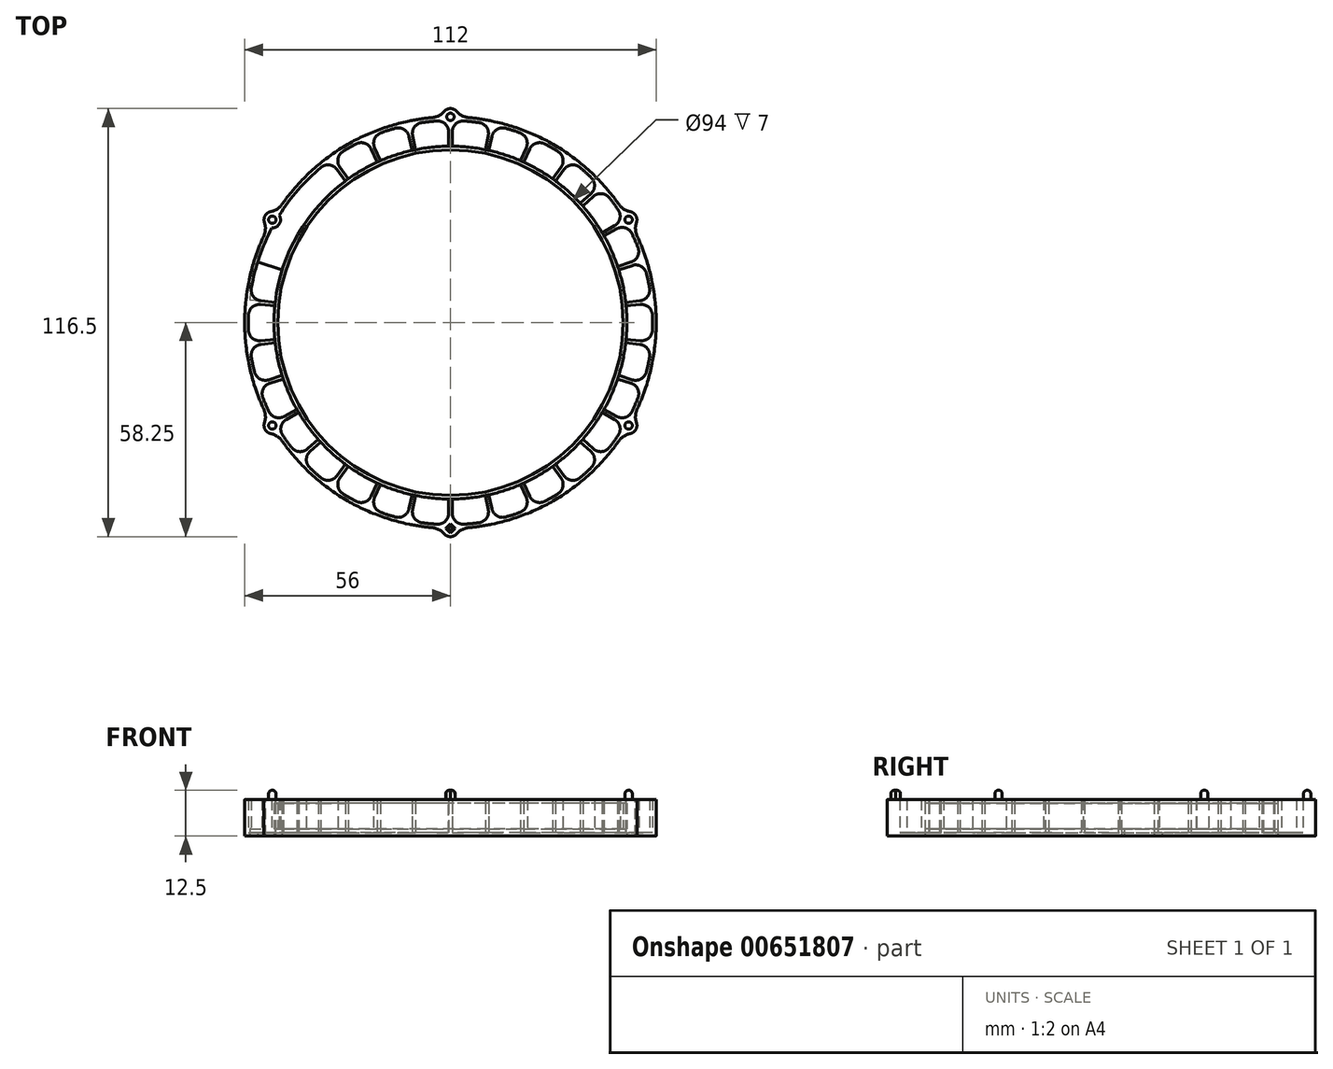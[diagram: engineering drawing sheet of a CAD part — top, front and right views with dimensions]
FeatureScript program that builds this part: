
annotation { "Feature Type Name" : "Feature", "Feature Type Description" : "" }
export const myFeature = defineFeature(function(context is Context, id is Id, definition is map)
    precondition{}
    {
        {
            var Q0;
            Q0=qCreatedBy(makeId("Top.planeOp"),FACE);
            var sketch = newSketch(context, id + "F0", { "sketchPlane" : qUnion([Q0])});
            skCircle(sketch, "E0", {"center": v(0, 0) * mm, "radius": 55 * mm});
            skCircle(sketch, "E1", {"center": v(0, 0) * mm, "radius": 56 * mm});
            skLineSegment(sketch, "E2", {"start": v(0, 60.2) * mm, "end": v(0, -62.26) * mm, "construction": true});
            skLineSegment(sketch, "E3", {"start": v(-62.84, 0) * mm, "end": v(64.36, 0) * mm, "construction": true});
            skLineSegment(sketch, "E4", {"start": v(55, 0) * mm, "end": v(56, 0) * mm});
            skCircle(sketch, "E5", {"center": v(0, 0) * mm, "radius": 48 * mm});
            skCircle(sketch, "E6", {"center": v(0, 0) * mm, "radius": 47 * mm});
            skLineSegment(sketch, "E7.left", {"start": v(-56, 0.5) * mm, "end": v(-56, -0.5) * mm});
            skLineSegment(sketch, "E7.right", {"start": v(56, 0.5) * mm, "end": v(56, -0.5) * mm});
            skLineSegment(sketch, "E8.bottom", {"start": v(0.5, -56) * mm, "end": v(-0.5, -56) * mm});
            skLineSegment(sketch, "E8.top", {"start": v(0.5, 56) * mm, "end": v(-0.5, 56) * mm});
            skLineSegment(sketch, "E8.left", {"start": v(0.5, -56) * mm, "end": v(0.5, 56) * mm});
            skLineSegment(sketch, "E8.right", {"start": v(-0.5, -56) * mm, "end": v(-0.5, 56) * mm});
            skLineSegment(sketch, "E9.bottom", {"start": v(12.13, 54.67) * mm, "end": v(-11.15, -54.88) * mm});
            skLineSegment(sketch, "E9.top", {"start": v(11.15, 54.88) * mm, "end": v(-12.13, -54.67) * mm});
            skLineSegment(sketch, "E9.left", {"start": v(12.13, 54.67) * mm, "end": v(11.15, 54.88) * mm});
            skLineSegment(sketch, "E9.right", {"start": v(-11.15, -54.88) * mm, "end": v(-12.13, -54.67) * mm});
            skLineSegment(sketch, "E10.bottom", {"start": v(-22.32, -51.36) * mm, "end": v(-23.23, -50.95) * mm});
            skLineSegment(sketch, "E10.top", {"start": v(23.23, 50.95) * mm, "end": v(22.32, 51.36) * mm});
            skLineSegment(sketch, "E10.left", {"start": v(-22.32, -51.36) * mm, "end": v(23.23, 50.95) * mm});
            skLineSegment(sketch, "E10.right", {"start": v(-23.23, -50.95) * mm, "end": v(22.32, 51.36) * mm});
            skLineSegment(sketch, "E11.bottom", {"start": v(32.51, 45.6) * mm, "end": v(33.32, 45) * mm});
            skLineSegment(sketch, "E11.top", {"start": v(-33.32, -45) * mm, "end": v(-32.51, -45.6) * mm});
            skLineSegment(sketch, "E11.left", {"start": v(32.51, 45.6) * mm, "end": v(-33.32, -45) * mm});
            skLineSegment(sketch, "E11.right", {"start": v(33.32, 45) * mm, "end": v(-32.51, -45.6) * mm});
            skLineSegment(sketch, "E12.bottom", {"start": v(-41.28, -37.84) * mm, "end": v(-41.95, -37.1) * mm});
            skLineSegment(sketch, "E12.top", {"start": v(41.95, 37.1) * mm, "end": v(41.28, 37.84) * mm});
            skLineSegment(sketch, "E12.left", {"start": v(-41.28, -37.84) * mm, "end": v(41.95, 37.1) * mm});
            skLineSegment(sketch, "E12.right", {"start": v(-41.95, -37.1) * mm, "end": v(41.28, 37.84) * mm});
            skLineSegment(sketch, "E13.bottom", {"start": v(48.25, 28.43) * mm, "end": v(48.75, 27.57) * mm});
            skLineSegment(sketch, "E13.top", {"start": v(-48.75, -27.57) * mm, "end": v(-48.25, -28.43) * mm});
            skLineSegment(sketch, "E13.left", {"start": v(48.25, 28.43) * mm, "end": v(-48.75, -27.57) * mm});
            skLineSegment(sketch, "E13.right", {"start": v(48.75, 27.57) * mm, "end": v(-48.25, -28.43) * mm});
            skLineSegment(sketch, "E14.bottom", {"start": v(-53.1, -17.78) * mm, "end": v(-53.41, -16.83) * mm});
            skLineSegment(sketch, "E14.top", {"start": v(53.41, 16.83) * mm, "end": v(53.1, 17.78) * mm});
            skLineSegment(sketch, "E14.left", {"start": v(-53.1, -17.78) * mm, "end": v(53.41, 16.83) * mm});
            skLineSegment(sketch, "E14.right", {"start": v(-53.41, -16.83) * mm, "end": v(53.1, 17.78) * mm});
            skLineSegment(sketch, "E15.bottom", {"start": v(55.64, 6.35) * mm, "end": v(55.74, 5.36) * mm});
            skLineSegment(sketch, "E15.top", {"start": v(-55.74, -5.36) * mm, "end": v(-55.64, -6.35) * mm});
            skLineSegment(sketch, "E15.left", {"start": v(55.64, 6.35) * mm, "end": v(-55.74, -5.36) * mm});
            skLineSegment(sketch, "E15.right", {"start": v(55.74, 5.36) * mm, "end": v(-55.64, -6.35) * mm});
            skLineSegment(sketch, "E16.bottom", {"start": v(-55.74, 5.36) * mm, "end": v(-55.64, 6.35) * mm});
            skLineSegment(sketch, "E16.top", {"start": v(55.64, -6.35) * mm, "end": v(55.74, -5.36) * mm});
            skLineSegment(sketch, "E16.left", {"start": v(-55.74, 5.36) * mm, "end": v(55.64, -6.35) * mm});
            skLineSegment(sketch, "E16.right", {"start": v(-55.64, 6.35) * mm, "end": v(55.74, -5.36) * mm});
            skLineSegment(sketch, "E17.bottom", {"start": v(53.41, -16.83) * mm, "end": v(53.1, -17.78) * mm});
            skLineSegment(sketch, "E17.top", {"start": v(-53.1, 17.78) * mm, "end": v(-53.41, 16.83) * mm});
            skLineSegment(sketch, "E17.left", {"start": v(53.41, -16.83) * mm, "end": v(-53.1, 17.78) * mm});
            skLineSegment(sketch, "E17.right", {"start": v(53.1, -17.78) * mm, "end": v(-53.41, 16.83) * mm});
            skLineSegment(sketch, "E18.bottom", {"start": v(48.75, -27.57) * mm, "end": v(48.25, -28.43) * mm});
            skLineSegment(sketch, "E18.top", {"start": v(-48.25, 28.43) * mm, "end": v(-48.75, 27.57) * mm});
            skLineSegment(sketch, "E18.left", {"start": v(48.75, -27.57) * mm, "end": v(-48.25, 28.43) * mm});
            skLineSegment(sketch, "E18.right", {"start": v(48.25, -28.43) * mm, "end": v(-48.75, 27.57) * mm});
            skLineSegment(sketch, "E19.bottom", {"start": v(-41.95, 37.1) * mm, "end": v(-41.28, 37.84) * mm});
            skLineSegment(sketch, "E19.top", {"start": v(41.28, -37.84) * mm, "end": v(41.95, -37.1) * mm});
            skLineSegment(sketch, "E19.left", {"start": v(-41.95, 37.1) * mm, "end": v(41.28, -37.84) * mm});
            skLineSegment(sketch, "E19.right", {"start": v(-41.28, 37.84) * mm, "end": v(41.95, -37.1) * mm});
            skLineSegment(sketch, "E20.bottom", {"start": v(-33.32, 45) * mm, "end": v(-32.51, 45.6) * mm});
            skLineSegment(sketch, "E20.top", {"start": v(32.51, -45.6) * mm, "end": v(33.32, -45) * mm});
            skLineSegment(sketch, "E20.left", {"start": v(-33.32, 45) * mm, "end": v(32.51, -45.6) * mm});
            skLineSegment(sketch, "E20.right", {"start": v(-32.51, 45.6) * mm, "end": v(33.32, -45) * mm});
            skLineSegment(sketch, "E21.bottom", {"start": v(-23.23, 50.95) * mm, "end": v(-22.32, 51.36) * mm});
            skLineSegment(sketch, "E21.top", {"start": v(22.32, -51.36) * mm, "end": v(23.23, -50.95) * mm});
            skLineSegment(sketch, "E21.left", {"start": v(-23.23, 50.95) * mm, "end": v(22.32, -51.36) * mm});
            skLineSegment(sketch, "E21.right", {"start": v(-22.32, 51.36) * mm, "end": v(23.23, -50.95) * mm});
            skLineSegment(sketch, "E22.bottom", {"start": v(-12.13, 54.67) * mm, "end": v(-11.15, 54.88) * mm});
            skLineSegment(sketch, "E22.top", {"start": v(11.15, -54.88) * mm, "end": v(12.13, -54.67) * mm});
            skLineSegment(sketch, "E22.left", {"start": v(-12.13, 54.67) * mm, "end": v(11.15, -54.88) * mm});
            skLineSegment(sketch, "E22.right", {"start": v(-11.15, 54.88) * mm, "end": v(12.13, -54.67) * mm});
            skSolve(sketch);
        }
        {
            var Q0;
            {var subQ0=sQuery(id+"F0.wireOp",EDGE,"E7.left");Q0=makeQuery(id+"F0.imprint","IMPRINT",FACE,{"disambiguationData":[TD([[makeQuery(id+"F0.imprint","IMPRINT",EDGE,{"derivedFrom":subQ0}),1.0]])]});}
            var Q1;
            {var subQ5=sQuery(id+"F0.wireOp",EDGE,"E8.top");Q1=makeQuery(id+"F0.imprint","IMPRINT",FACE,{"disambiguationData":[TD([[makeQuery(id+"F0.imprint","IMPRINT",EDGE,{"derivedFrom":subQ5}),1.0]])]});}
            var Q2;
            {var subQ0=sQuery(id+"F0.wireOp",EDGE,"E9.top");var subQ1=sQuery(id+"F0.wireOp",EDGE,"E0");var subQ2=makeQuery(id+"F0.imprint","INTERSECT",VERTEX,{"disambiguationData":[OD(0.0)],"derivedFrom":[subQ1,subQ0]});Q2=makeQuery(id+"F0.imprint","IMPRINT",FACE,{"disambiguationData":[TD([[makeQuery(id+"F0.imprint","IMPRINT",EDGE,{"disambiguationData":[TD([[subQ2,-1.0]])],"derivedFrom":subQ1}),-1.0]])]});}
            var Q3;
            {var subQ5=sQuery(id+"F0.wireOp",EDGE,"E9.left");Q3=makeQuery(id+"F0.imprint","IMPRINT",FACE,{"disambiguationData":[TD([[makeQuery(id+"F0.imprint","IMPRINT",EDGE,{"derivedFrom":subQ5}),1.0]])]});}
            var Q4;
            {var subQ0=sQuery(id+"F0.wireOp",EDGE,"E10.right");var subQ1=sQuery(id+"F0.wireOp",EDGE,"E0");var subQ2=makeQuery(id+"F0.imprint","INTERSECT",VERTEX,{"disambiguationData":[OD(0.0)],"derivedFrom":[subQ1,subQ0]});Q4=makeQuery(id+"F0.imprint","IMPRINT",FACE,{"disambiguationData":[TD([[makeQuery(id+"F0.imprint","IMPRINT",EDGE,{"disambiguationData":[TD([[subQ2,-1.0]])],"derivedFrom":subQ1}),-1.0]])]});}
            var Q5;
            {var subQ5=sQuery(id+"F0.wireOp",EDGE,"E10.top");Q5=makeQuery(id+"F0.imprint","IMPRINT",FACE,{"disambiguationData":[TD([[makeQuery(id+"F0.imprint","IMPRINT",EDGE,{"derivedFrom":subQ5}),1.0]])]});}
            var Q6;
            {var subQ0=sQuery(id+"F0.wireOp",EDGE,"E11.left");var subQ1=sQuery(id+"F0.wireOp",EDGE,"E0");var subQ2=makeQuery(id+"F0.imprint","INTERSECT",VERTEX,{"disambiguationData":[OD(0.0)],"derivedFrom":[subQ1,subQ0]});Q6=makeQuery(id+"F0.imprint","IMPRINT",FACE,{"disambiguationData":[TD([[makeQuery(id+"F0.imprint","IMPRINT",EDGE,{"disambiguationData":[TD([[subQ2,-1.0]])],"derivedFrom":subQ1}),-1.0]])]});}
            var Q7;
            {var subQ3=sQuery(id+"F0.wireOp",EDGE,"E4");var subQ7=sQuery(id+"F0.wireOp",EDGE,"E0");var subQ8=makeQuery(id+"F0.imprint","INTERSECT",VERTEX,{"derivedFrom":[subQ7,subQ3]});Q7=makeQuery(id+"F0.imprint","IMPRINT",FACE,{"disambiguationData":[TD([[makeQuery(id+"F0.imprint","IMPRINT",EDGE,{"disambiguationData":[TD([[subQ8,-1.0]])],"derivedFrom":subQ7}),-1.0]])]});}
            var Q8;
            {var subQ5=sQuery(id+"F0.wireOp",EDGE,"E11.bottom");Q8=makeQuery(id+"F0.imprint","IMPRINT",FACE,{"disambiguationData":[TD([[makeQuery(id+"F0.imprint","IMPRINT",EDGE,{"derivedFrom":subQ5}),-1.0]])]});}
            var Q9;
            {var subQ3=sQuery(id+"F0.wireOp",EDGE,"E4");var subQ5=sQuery(id+"F0.wireOp",EDGE,"E0");var subQ6=makeQuery(id+"F0.imprint","INTERSECT",VERTEX,{"derivedFrom":[subQ5,subQ3]});Q9=makeQuery(id+"F0.imprint","IMPRINT",FACE,{"disambiguationData":[TD([[makeQuery(id+"F0.imprint","IMPRINT",EDGE,{"disambiguationData":[TD([[subQ6,1.0]])],"derivedFrom":subQ5}),-1.0]])]});}
            var Q10;
            {var subQ5=sQuery(id+"F0.wireOp",EDGE,"E8.bottom");Q10=makeQuery(id+"F0.imprint","IMPRINT",FACE,{"disambiguationData":[TD([[makeQuery(id+"F0.imprint","IMPRINT",EDGE,{"derivedFrom":subQ5}),-1.0]])]});}
            var Q11;
            {var subQ0=sQuery(id+"F0.wireOp",EDGE,"E11.right");var subQ1=sQuery(id+"F0.wireOp",EDGE,"E0");var subQ2=makeQuery(id+"F0.imprint","INTERSECT",VERTEX,{"disambiguationData":[OD(1.0)],"derivedFrom":[subQ1,subQ0]});Q11=makeQuery(id+"F0.imprint","IMPRINT",FACE,{"disambiguationData":[TD([[makeQuery(id+"F0.imprint","IMPRINT",EDGE,{"disambiguationData":[TD([[subQ2,-1.0]])],"derivedFrom":subQ1}),-1.0]])]});}
            var Q12;
            {var subQ5=sQuery(id+"F0.wireOp",EDGE,"E11.top");Q12=makeQuery(id+"F0.imprint","IMPRINT",FACE,{"disambiguationData":[TD([[makeQuery(id+"F0.imprint","IMPRINT",EDGE,{"derivedFrom":subQ5}),1.0]])]});}
            var Q13;
            {var subQ5=sQuery(id+"F0.wireOp",EDGE,"E10.bottom");Q13=makeQuery(id+"F0.imprint","IMPRINT",FACE,{"disambiguationData":[TD([[makeQuery(id+"F0.imprint","IMPRINT",EDGE,{"derivedFrom":subQ5}),-1.0]])]});}
            var Q14;
            {var subQ0=sQuery(id+"F0.wireOp",EDGE,"E10.left");var subQ1=sQuery(id+"F0.wireOp",EDGE,"E0");var subQ2=makeQuery(id+"F0.imprint","INTERSECT",VERTEX,{"disambiguationData":[OD(1.0)],"derivedFrom":[subQ1,subQ0]});Q14=makeQuery(id+"F0.imprint","IMPRINT",FACE,{"disambiguationData":[TD([[makeQuery(id+"F0.imprint","IMPRINT",EDGE,{"disambiguationData":[TD([[subQ2,-1.0]])],"derivedFrom":subQ1}),-1.0]])]});}
            var Q15;
            {var subQ5=sQuery(id+"F0.wireOp",EDGE,"E9.right");Q15=makeQuery(id+"F0.imprint","IMPRINT",FACE,{"disambiguationData":[TD([[makeQuery(id+"F0.imprint","IMPRINT",EDGE,{"derivedFrom":subQ5}),-1.0]])]});}
            var Q16;
            {var subQ0=sQuery(id+"F0.wireOp",EDGE,"E9.bottom");var subQ1=sQuery(id+"F0.wireOp",EDGE,"E0");var subQ2=makeQuery(id+"F0.imprint","INTERSECT",VERTEX,{"disambiguationData":[OD(1.0)],"derivedFrom":[subQ1,subQ0]});Q16=makeQuery(id+"F0.imprint","IMPRINT",FACE,{"disambiguationData":[TD([[makeQuery(id+"F0.imprint","IMPRINT",EDGE,{"disambiguationData":[TD([[subQ2,-1.0]])],"derivedFrom":subQ1}),-1.0]])]});}
            var Q17;
            {var subQ0=sQuery(id+"F0.wireOp",EDGE,"E8.left");var subQ1=sQuery(id+"F0.wireOp",EDGE,"E0");var subQ2=makeQuery(id+"F0.imprint","INTERSECT",VERTEX,{"disambiguationData":[OD(0.0)],"derivedFrom":[subQ1,subQ0]});Q17=makeQuery(id+"F0.imprint","IMPRINT",FACE,{"disambiguationData":[TD([[makeQuery(id+"F0.imprint","IMPRINT",EDGE,{"disambiguationData":[TD([[subQ2,-1.0]])],"derivedFrom":subQ1}),1.0]])]});}
            var Q18;
            {var subQ0=sQuery(id+"F0.wireOp",EDGE,"E9.bottom");var subQ1=sQuery(id+"F0.wireOp",EDGE,"E0");var subQ2=makeQuery(id+"F0.imprint","INTERSECT",VERTEX,{"disambiguationData":[OD(0.0)],"derivedFrom":[subQ1,subQ0]});Q18=makeQuery(id+"F0.imprint","IMPRINT",FACE,{"disambiguationData":[TD([[makeQuery(id+"F0.imprint","IMPRINT",EDGE,{"disambiguationData":[TD([[subQ2,-1.0]])],"derivedFrom":subQ1}),1.0]])]});}
            var Q19;
            {var subQ0=sQuery(id+"F0.wireOp",EDGE,"E10.left");var subQ1=sQuery(id+"F0.wireOp",EDGE,"E0");var subQ2=makeQuery(id+"F0.imprint","INTERSECT",VERTEX,{"disambiguationData":[OD(0.0)],"derivedFrom":[subQ1,subQ0]});Q19=makeQuery(id+"F0.imprint","IMPRINT",FACE,{"disambiguationData":[TD([[makeQuery(id+"F0.imprint","IMPRINT",EDGE,{"disambiguationData":[TD([[subQ2,-1.0]])],"derivedFrom":subQ1}),1.0]])]});}
            var Q20;
            {var subQ0=sQuery(id+"F0.wireOp",EDGE,"E11.right");var subQ1=sQuery(id+"F0.wireOp",EDGE,"E0");var subQ2=makeQuery(id+"F0.imprint","INTERSECT",VERTEX,{"disambiguationData":[OD(0.0)],"derivedFrom":[subQ1,subQ0]});Q20=makeQuery(id+"F0.imprint","IMPRINT",FACE,{"disambiguationData":[TD([[makeQuery(id+"F0.imprint","IMPRINT",EDGE,{"disambiguationData":[TD([[subQ2,-1.0]])],"derivedFrom":subQ1}),1.0]])]});}
            var Q21;
            {var subQ0=sQuery(id+"F0.wireOp",EDGE,"E8.right");var subQ1=sQuery(id+"F0.wireOp",EDGE,"E0");var subQ2=makeQuery(id+"F0.imprint","INTERSECT",VERTEX,{"disambiguationData":[OD(1.0)],"derivedFrom":[subQ1,subQ0]});Q21=makeQuery(id+"F0.imprint","IMPRINT",FACE,{"disambiguationData":[TD([[makeQuery(id+"F0.imprint","IMPRINT",EDGE,{"disambiguationData":[TD([[subQ2,-1.0]])],"derivedFrom":subQ1}),1.0]])]});}
            var Q22;
            {var subQ0=sQuery(id+"F0.wireOp",EDGE,"E11.left");var subQ1=sQuery(id+"F0.wireOp",EDGE,"E0");var subQ2=makeQuery(id+"F0.imprint","INTERSECT",VERTEX,{"disambiguationData":[OD(1.0)],"derivedFrom":[subQ1,subQ0]});Q22=makeQuery(id+"F0.imprint","IMPRINT",FACE,{"disambiguationData":[TD([[makeQuery(id+"F0.imprint","IMPRINT",EDGE,{"disambiguationData":[TD([[subQ2,-1.0]])],"derivedFrom":subQ1}),1.0]])]});}
            var Q23;
            {var subQ0=sQuery(id+"F0.wireOp",EDGE,"E10.right");var subQ1=sQuery(id+"F0.wireOp",EDGE,"E0");var subQ2=makeQuery(id+"F0.imprint","INTERSECT",VERTEX,{"disambiguationData":[OD(1.0)],"derivedFrom":[subQ1,subQ0]});Q23=makeQuery(id+"F0.imprint","IMPRINT",FACE,{"disambiguationData":[TD([[makeQuery(id+"F0.imprint","IMPRINT",EDGE,{"disambiguationData":[TD([[subQ2,-1.0]])],"derivedFrom":subQ1}),1.0]])]});}
            var Q24;
            {var subQ0=sQuery(id+"F0.wireOp",EDGE,"E9.top");var subQ1=sQuery(id+"F0.wireOp",EDGE,"E0");var subQ2=makeQuery(id+"F0.imprint","INTERSECT",VERTEX,{"disambiguationData":[OD(1.0)],"derivedFrom":[subQ1,subQ0]});Q24=makeQuery(id+"F0.imprint","IMPRINT",FACE,{"disambiguationData":[TD([[makeQuery(id+"F0.imprint","IMPRINT",EDGE,{"disambiguationData":[TD([[subQ2,-1.0]])],"derivedFrom":subQ1}),1.0]])]});}
            var Q25;
            {var subQ0=sQuery(id+"F0.wireOp",EDGE,"E12.left");var subQ1=sQuery(id+"F0.wireOp",EDGE,"E0");var subQ2=makeQuery(id+"F0.imprint","INTERSECT",VERTEX,{"disambiguationData":[OD(1.0)],"derivedFrom":[subQ1,subQ0]});Q25=makeQuery(id+"F0.imprint","IMPRINT",FACE,{"disambiguationData":[TD([[makeQuery(id+"F0.imprint","IMPRINT",EDGE,{"disambiguationData":[TD([[subQ2,-1.0]])],"derivedFrom":subQ1}),-1.0]])]});}
            var Q26;
            {var subQ5=sQuery(id+"F0.wireOp",EDGE,"E12.bottom");Q26=makeQuery(id+"F0.imprint","IMPRINT",FACE,{"disambiguationData":[TD([[makeQuery(id+"F0.imprint","IMPRINT",EDGE,{"derivedFrom":subQ5}),-1.0]])]});}
            var Q27;
            {var subQ0=sQuery(id+"F0.wireOp",EDGE,"E13.right");var subQ1=sQuery(id+"F0.wireOp",EDGE,"E0");var subQ2=makeQuery(id+"F0.imprint","INTERSECT",VERTEX,{"disambiguationData":[OD(1.0)],"derivedFrom":[subQ1,subQ0]});Q27=makeQuery(id+"F0.imprint","IMPRINT",FACE,{"disambiguationData":[TD([[makeQuery(id+"F0.imprint","IMPRINT",EDGE,{"disambiguationData":[TD([[subQ2,-1.0]])],"derivedFrom":subQ1}),-1.0]])]});}
            var Q28;
            {var subQ5=sQuery(id+"F0.wireOp",EDGE,"E13.top");Q28=makeQuery(id+"F0.imprint","IMPRINT",FACE,{"disambiguationData":[TD([[makeQuery(id+"F0.imprint","IMPRINT",EDGE,{"derivedFrom":subQ5}),1.0]])]});}
            var Q29;
            {var subQ0=sQuery(id+"F0.wireOp",EDGE,"E14.left");var subQ1=sQuery(id+"F0.wireOp",EDGE,"E0");var subQ2=makeQuery(id+"F0.imprint","INTERSECT",VERTEX,{"disambiguationData":[OD(1.0)],"derivedFrom":[subQ1,subQ0]});Q29=makeQuery(id+"F0.imprint","IMPRINT",FACE,{"disambiguationData":[TD([[makeQuery(id+"F0.imprint","IMPRINT",EDGE,{"disambiguationData":[TD([[subQ2,-1.0]])],"derivedFrom":subQ1}),-1.0]])]});}
            var Q30;
            {var subQ0=sQuery(id+"F0.wireOp",EDGE,"E8.left");var subQ1=sQuery(id+"F0.wireOp",EDGE,"E0");var subQ2=makeQuery(id+"F0.imprint","INTERSECT",VERTEX,{"disambiguationData":[OD(1.0)],"derivedFrom":[subQ1,subQ0]});Q30=makeQuery(id+"F0.imprint","IMPRINT",FACE,{"disambiguationData":[TD([[makeQuery(id+"F0.imprint","IMPRINT",EDGE,{"disambiguationData":[TD([[subQ2,-1.0]])],"derivedFrom":subQ1}),-1.0]])]});}
            var Q31;
            {var subQ0=sQuery(id+"F0.wireOp",EDGE,"E22.right");var subQ1=sQuery(id+"F0.wireOp",EDGE,"E0");var subQ2=makeQuery(id+"F0.imprint","INTERSECT",VERTEX,{"disambiguationData":[OD(1.0)],"derivedFrom":[subQ1,subQ0]});Q31=makeQuery(id+"F0.imprint","IMPRINT",FACE,{"disambiguationData":[TD([[makeQuery(id+"F0.imprint","IMPRINT",EDGE,{"disambiguationData":[TD([[subQ2,-1.0]])],"derivedFrom":subQ1}),-1.0]])]});}
            var Q32;
            {var subQ0=sQuery(id+"F0.wireOp",EDGE,"E21.right");var subQ1=sQuery(id+"F0.wireOp",EDGE,"E0");var subQ2=makeQuery(id+"F0.imprint","INTERSECT",VERTEX,{"disambiguationData":[OD(1.0)],"derivedFrom":[subQ1,subQ0]});Q32=makeQuery(id+"F0.imprint","IMPRINT",FACE,{"disambiguationData":[TD([[makeQuery(id+"F0.imprint","IMPRINT",EDGE,{"disambiguationData":[TD([[subQ2,-1.0]])],"derivedFrom":subQ1}),-1.0]])]});}
            var Q33;
            {var subQ0=sQuery(id+"F0.wireOp",EDGE,"E20.right");var subQ1=sQuery(id+"F0.wireOp",EDGE,"E0");var subQ2=makeQuery(id+"F0.imprint","INTERSECT",VERTEX,{"disambiguationData":[OD(1.0)],"derivedFrom":[subQ1,subQ0]});Q33=makeQuery(id+"F0.imprint","IMPRINT",FACE,{"disambiguationData":[TD([[makeQuery(id+"F0.imprint","IMPRINT",EDGE,{"disambiguationData":[TD([[subQ2,-1.0]])],"derivedFrom":subQ1}),-1.0]])]});}
            var Q34;
            {var subQ0=sQuery(id+"F0.wireOp",EDGE,"E19.right");var subQ1=sQuery(id+"F0.wireOp",EDGE,"E0");var subQ2=makeQuery(id+"F0.imprint","INTERSECT",VERTEX,{"disambiguationData":[OD(1.0)],"derivedFrom":[subQ1,subQ0]});Q34=makeQuery(id+"F0.imprint","IMPRINT",FACE,{"disambiguationData":[TD([[makeQuery(id+"F0.imprint","IMPRINT",EDGE,{"disambiguationData":[TD([[subQ2,-1.0]])],"derivedFrom":subQ1}),-1.0]])]});}
            var Q35;
            {var subQ0=sQuery(id+"F0.wireOp",EDGE,"E18.left");var subQ1=sQuery(id+"F0.wireOp",EDGE,"E0");var subQ2=makeQuery(id+"F0.imprint","INTERSECT",VERTEX,{"disambiguationData":[OD(1.0)],"derivedFrom":[subQ1,subQ0]});Q35=makeQuery(id+"F0.imprint","IMPRINT",FACE,{"disambiguationData":[TD([[makeQuery(id+"F0.imprint","IMPRINT",EDGE,{"disambiguationData":[TD([[subQ2,-1.0]])],"derivedFrom":subQ1}),-1.0]])]});}
            var Q36;
            {var subQ0=sQuery(id+"F0.wireOp",EDGE,"E17.left");var subQ1=sQuery(id+"F0.wireOp",EDGE,"E0");var subQ2=makeQuery(id+"F0.imprint","INTERSECT",VERTEX,{"disambiguationData":[OD(1.0)],"derivedFrom":[subQ1,subQ0]});Q36=makeQuery(id+"F0.imprint","IMPRINT",FACE,{"disambiguationData":[TD([[makeQuery(id+"F0.imprint","IMPRINT",EDGE,{"disambiguationData":[TD([[subQ2,-1.0]])],"derivedFrom":subQ1}),-1.0]])]});}
            var Q37;
            {var subQ5=sQuery(id+"F0.wireOp",EDGE,"E22.top");Q37=makeQuery(id+"F0.imprint","IMPRINT",FACE,{"disambiguationData":[TD([[makeQuery(id+"F0.imprint","IMPRINT",EDGE,{"derivedFrom":subQ5}),1.0]])]});}
            var Q38;
            {var subQ5=sQuery(id+"F0.wireOp",EDGE,"E21.top");Q38=makeQuery(id+"F0.imprint","IMPRINT",FACE,{"disambiguationData":[TD([[makeQuery(id+"F0.imprint","IMPRINT",EDGE,{"derivedFrom":subQ5}),1.0]])]});}
            var Q39;
            {var subQ5=sQuery(id+"F0.wireOp",EDGE,"E20.top");Q39=makeQuery(id+"F0.imprint","IMPRINT",FACE,{"disambiguationData":[TD([[makeQuery(id+"F0.imprint","IMPRINT",EDGE,{"derivedFrom":subQ5}),1.0]])]});}
            var Q40;
            {var subQ5=sQuery(id+"F0.wireOp",EDGE,"E19.top");Q40=makeQuery(id+"F0.imprint","IMPRINT",FACE,{"disambiguationData":[TD([[makeQuery(id+"F0.imprint","IMPRINT",EDGE,{"derivedFrom":subQ5}),1.0]])]});}
            var Q41;
            {var subQ5=sQuery(id+"F0.wireOp",EDGE,"E18.bottom");Q41=makeQuery(id+"F0.imprint","IMPRINT",FACE,{"disambiguationData":[TD([[makeQuery(id+"F0.imprint","IMPRINT",EDGE,{"derivedFrom":subQ5}),-1.0]])]});}
            var Q42;
            {var subQ5=sQuery(id+"F0.wireOp",EDGE,"E17.bottom");Q42=makeQuery(id+"F0.imprint","IMPRINT",FACE,{"disambiguationData":[TD([[makeQuery(id+"F0.imprint","IMPRINT",EDGE,{"derivedFrom":subQ5}),-1.0]])]});}
            var Q43;
            {var subQ5=sQuery(id+"F0.wireOp",EDGE,"E16.top");Q43=makeQuery(id+"F0.imprint","IMPRINT",FACE,{"disambiguationData":[TD([[makeQuery(id+"F0.imprint","IMPRINT",EDGE,{"derivedFrom":subQ5}),1.0]])]});}
            var Q44;
            {var subQ5=sQuery(id+"F0.wireOp",EDGE,"E15.bottom");Q44=makeQuery(id+"F0.imprint","IMPRINT",FACE,{"disambiguationData":[TD([[makeQuery(id+"F0.imprint","IMPRINT",EDGE,{"derivedFrom":subQ5}),-1.0]])]});}
            var Q45;
            {var subQ5=sQuery(id+"F0.wireOp",EDGE,"E14.top");Q45=makeQuery(id+"F0.imprint","IMPRINT",FACE,{"disambiguationData":[TD([[makeQuery(id+"F0.imprint","IMPRINT",EDGE,{"derivedFrom":subQ5}),1.0]])]});}
            var Q46;
            {var subQ0=sQuery(id+"F0.wireOp",EDGE,"E14.right");var subQ1=sQuery(id+"F0.wireOp",EDGE,"E0");var subQ2=makeQuery(id+"F0.imprint","INTERSECT",VERTEX,{"disambiguationData":[OD(0.0)],"derivedFrom":[subQ1,subQ0]});Q46=makeQuery(id+"F0.imprint","IMPRINT",FACE,{"disambiguationData":[TD([[makeQuery(id+"F0.imprint","IMPRINT",EDGE,{"disambiguationData":[TD([[subQ2,-1.0]])],"derivedFrom":subQ1}),-1.0]])]});}
            var Q47;
            {var subQ0=sQuery(id+"F0.wireOp",EDGE,"E12.right");var subQ1=sQuery(id+"F0.wireOp",EDGE,"E0");var subQ2=makeQuery(id+"F0.imprint","INTERSECT",VERTEX,{"disambiguationData":[OD(0.0)],"derivedFrom":[subQ1,subQ0]});Q47=makeQuery(id+"F0.imprint","IMPRINT",FACE,{"disambiguationData":[TD([[makeQuery(id+"F0.imprint","IMPRINT",EDGE,{"disambiguationData":[TD([[subQ2,-1.0]])],"derivedFrom":subQ1}),-1.0]])]});}
            var Q48;
            {var subQ5=sQuery(id+"F0.wireOp",EDGE,"E12.top");Q48=makeQuery(id+"F0.imprint","IMPRINT",FACE,{"disambiguationData":[TD([[makeQuery(id+"F0.imprint","IMPRINT",EDGE,{"derivedFrom":subQ5}),1.0]])]});}
            var Q49;
            {var subQ0=sQuery(id+"F0.wireOp",EDGE,"E13.left");var subQ1=sQuery(id+"F0.wireOp",EDGE,"E0");var subQ2=makeQuery(id+"F0.imprint","INTERSECT",VERTEX,{"disambiguationData":[OD(0.0)],"derivedFrom":[subQ1,subQ0]});Q49=makeQuery(id+"F0.imprint","IMPRINT",FACE,{"disambiguationData":[TD([[makeQuery(id+"F0.imprint","IMPRINT",EDGE,{"disambiguationData":[TD([[subQ2,-1.0]])],"derivedFrom":subQ1}),-1.0]])]});}
            var Q50;
            {var subQ5=sQuery(id+"F0.wireOp",EDGE,"E13.bottom");Q50=makeQuery(id+"F0.imprint","IMPRINT",FACE,{"disambiguationData":[TD([[makeQuery(id+"F0.imprint","IMPRINT",EDGE,{"derivedFrom":subQ5}),-1.0]])]});}
            var Q51;
            {var subQ0=sQuery(id+"F0.wireOp",EDGE,"E15.left");var subQ1=sQuery(id+"F0.wireOp",EDGE,"E0");var subQ2=makeQuery(id+"F0.imprint","INTERSECT",VERTEX,{"disambiguationData":[OD(0.0)],"derivedFrom":[subQ1,subQ0]});Q51=makeQuery(id+"F0.imprint","IMPRINT",FACE,{"disambiguationData":[TD([[makeQuery(id+"F0.imprint","IMPRINT",EDGE,{"disambiguationData":[TD([[subQ2,-1.0]])],"derivedFrom":subQ1}),-1.0]])]});}
            var Q52;
            {var subQ0=sQuery(id+"F0.wireOp",EDGE,"E16.left");var subQ1=sQuery(id+"F0.wireOp",EDGE,"E0");var subQ2=makeQuery(id+"F0.imprint","INTERSECT",VERTEX,{"disambiguationData":[OD(1.0)],"derivedFrom":[subQ1,subQ0]});Q52=makeQuery(id+"F0.imprint","IMPRINT",FACE,{"disambiguationData":[TD([[makeQuery(id+"F0.imprint","IMPRINT",EDGE,{"disambiguationData":[TD([[subQ2,-1.0]])],"derivedFrom":subQ1}),1.0]])]});}
            var Q53;
            {var subQ0=sQuery(id+"F0.wireOp",EDGE,"E15.right");var subQ1=sQuery(id+"F0.wireOp",EDGE,"E0");var subQ2=makeQuery(id+"F0.imprint","INTERSECT",VERTEX,{"disambiguationData":[OD(0.0)],"derivedFrom":[subQ1,subQ0]});Q53=makeQuery(id+"F0.imprint","IMPRINT",FACE,{"disambiguationData":[TD([[makeQuery(id+"F0.imprint","IMPRINT",EDGE,{"disambiguationData":[TD([[subQ2,-1.0]])],"derivedFrom":subQ1}),1.0]])]});}
            var Q54;
            {var subQ0=sQuery(id+"F0.wireOp",EDGE,"E14.left");var subQ1=sQuery(id+"F0.wireOp",EDGE,"E0");var subQ2=makeQuery(id+"F0.imprint","INTERSECT",VERTEX,{"disambiguationData":[OD(0.0)],"derivedFrom":[subQ1,subQ0]});Q54=makeQuery(id+"F0.imprint","IMPRINT",FACE,{"disambiguationData":[TD([[makeQuery(id+"F0.imprint","IMPRINT",EDGE,{"disambiguationData":[TD([[subQ2,-1.0]])],"derivedFrom":subQ1}),1.0]])]});}
            var Q55;
            {var subQ0=sQuery(id+"F0.wireOp",EDGE,"E13.right");var subQ1=sQuery(id+"F0.wireOp",EDGE,"E0");var subQ2=makeQuery(id+"F0.imprint","INTERSECT",VERTEX,{"disambiguationData":[OD(0.0)],"derivedFrom":[subQ1,subQ0]});Q55=makeQuery(id+"F0.imprint","IMPRINT",FACE,{"disambiguationData":[TD([[makeQuery(id+"F0.imprint","IMPRINT",EDGE,{"disambiguationData":[TD([[subQ2,-1.0]])],"derivedFrom":subQ1}),1.0]])]});}
            var Q56;
            {var subQ0=sQuery(id+"F0.wireOp",EDGE,"E12.left");var subQ1=sQuery(id+"F0.wireOp",EDGE,"E0");var subQ2=makeQuery(id+"F0.imprint","INTERSECT",VERTEX,{"disambiguationData":[OD(0.0)],"derivedFrom":[subQ1,subQ0]});Q56=makeQuery(id+"F0.imprint","IMPRINT",FACE,{"disambiguationData":[TD([[makeQuery(id+"F0.imprint","IMPRINT",EDGE,{"disambiguationData":[TD([[subQ2,-1.0]])],"derivedFrom":subQ1}),1.0]])]});}
            var Q57;
            {var subQ0=sQuery(id+"F0.wireOp",EDGE,"E8.right");var subQ1=sQuery(id+"F0.wireOp",EDGE,"E0");var subQ2=makeQuery(id+"F0.imprint","INTERSECT",VERTEX,{"disambiguationData":[OD(0.0)],"derivedFrom":[subQ1,subQ0]});Q57=makeQuery(id+"F0.imprint","IMPRINT",FACE,{"disambiguationData":[TD([[makeQuery(id+"F0.imprint","IMPRINT",EDGE,{"disambiguationData":[TD([[subQ2,-1.0]])],"derivedFrom":subQ1}),-1.0]])]});}
            var Q58;
            {var subQ5=sQuery(id+"F0.wireOp",EDGE,"E22.bottom");Q58=makeQuery(id+"F0.imprint","IMPRINT",FACE,{"disambiguationData":[TD([[makeQuery(id+"F0.imprint","IMPRINT",EDGE,{"derivedFrom":subQ5}),-1.0]])]});}
            var Q59;
            {var subQ5=sQuery(id+"F0.wireOp",EDGE,"E21.bottom");Q59=makeQuery(id+"F0.imprint","IMPRINT",FACE,{"disambiguationData":[TD([[makeQuery(id+"F0.imprint","IMPRINT",EDGE,{"derivedFrom":subQ5}),-1.0]])]});}
            var Q60;
            {var subQ0=sQuery(id+"F0.wireOp",EDGE,"E22.left");var subQ1=sQuery(id+"F0.wireOp",EDGE,"E0");var subQ2=makeQuery(id+"F0.imprint","INTERSECT",VERTEX,{"disambiguationData":[OD(0.0)],"derivedFrom":[subQ1,subQ0]});Q60=makeQuery(id+"F0.imprint","IMPRINT",FACE,{"disambiguationData":[TD([[makeQuery(id+"F0.imprint","IMPRINT",EDGE,{"disambiguationData":[TD([[subQ2,-1.0]])],"derivedFrom":subQ1}),-1.0]])]});}
            var Q61;
            {var subQ0=sQuery(id+"F0.wireOp",EDGE,"E21.left");var subQ1=sQuery(id+"F0.wireOp",EDGE,"E0");var subQ2=makeQuery(id+"F0.imprint","INTERSECT",VERTEX,{"disambiguationData":[OD(0.0)],"derivedFrom":[subQ1,subQ0]});Q61=makeQuery(id+"F0.imprint","IMPRINT",FACE,{"disambiguationData":[TD([[makeQuery(id+"F0.imprint","IMPRINT",EDGE,{"disambiguationData":[TD([[subQ2,-1.0]])],"derivedFrom":subQ1}),-1.0]])]});}
            var Q62;
            {var subQ5=sQuery(id+"F0.wireOp",EDGE,"E20.bottom");Q62=makeQuery(id+"F0.imprint","IMPRINT",FACE,{"disambiguationData":[TD([[makeQuery(id+"F0.imprint","IMPRINT",EDGE,{"derivedFrom":subQ5}),-1.0]])]});}
            var Q63;
            {var subQ0=sQuery(id+"F0.wireOp",EDGE,"E20.left");var subQ1=sQuery(id+"F0.wireOp",EDGE,"E0");var subQ2=makeQuery(id+"F0.imprint","INTERSECT",VERTEX,{"disambiguationData":[OD(0.0)],"derivedFrom":[subQ1,subQ0]});Q63=makeQuery(id+"F0.imprint","IMPRINT",FACE,{"disambiguationData":[TD([[makeQuery(id+"F0.imprint","IMPRINT",EDGE,{"disambiguationData":[TD([[subQ2,-1.0]])],"derivedFrom":subQ1}),-1.0]])]});}
            var Q64;
            {var subQ0=sQuery(id+"F0.wireOp",EDGE,"E19.left");var subQ1=sQuery(id+"F0.wireOp",EDGE,"E0");var subQ2=makeQuery(id+"F0.imprint","INTERSECT",VERTEX,{"disambiguationData":[OD(0.0)],"derivedFrom":[subQ1,subQ0]});Q64=makeQuery(id+"F0.imprint","IMPRINT",FACE,{"disambiguationData":[TD([[makeQuery(id+"F0.imprint","IMPRINT",EDGE,{"disambiguationData":[TD([[subQ2,-1.0]])],"derivedFrom":subQ1}),-1.0]])]});}
            var Q65;
            {var subQ5=sQuery(id+"F0.wireOp",EDGE,"E19.bottom");Q65=makeQuery(id+"F0.imprint","IMPRINT",FACE,{"disambiguationData":[TD([[makeQuery(id+"F0.imprint","IMPRINT",EDGE,{"derivedFrom":subQ5}),-1.0]])]});}
            var Q66;
            {var subQ0=sQuery(id+"F0.wireOp",EDGE,"E20.right");var subQ1=sQuery(id+"F0.wireOp",EDGE,"E0");var subQ2=makeQuery(id+"F0.imprint","INTERSECT",VERTEX,{"disambiguationData":[OD(0.0)],"derivedFrom":[subQ1,subQ0]});Q66=makeQuery(id+"F0.imprint","IMPRINT",FACE,{"disambiguationData":[TD([[makeQuery(id+"F0.imprint","IMPRINT",EDGE,{"disambiguationData":[TD([[subQ2,-1.0]])],"derivedFrom":subQ1}),1.0]])]});}
            var Q67;
            {var subQ0=sQuery(id+"F0.wireOp",EDGE,"E21.right");var subQ1=sQuery(id+"F0.wireOp",EDGE,"E0");var subQ2=makeQuery(id+"F0.imprint","INTERSECT",VERTEX,{"disambiguationData":[OD(0.0)],"derivedFrom":[subQ1,subQ0]});Q67=makeQuery(id+"F0.imprint","IMPRINT",FACE,{"disambiguationData":[TD([[makeQuery(id+"F0.imprint","IMPRINT",EDGE,{"disambiguationData":[TD([[subQ2,-1.0]])],"derivedFrom":subQ1}),1.0]])]});}
            var Q68;
            {var subQ0=sQuery(id+"F0.wireOp",EDGE,"E22.right");var subQ1=sQuery(id+"F0.wireOp",EDGE,"E0");var subQ2=makeQuery(id+"F0.imprint","INTERSECT",VERTEX,{"disambiguationData":[OD(0.0)],"derivedFrom":[subQ1,subQ0]});Q68=makeQuery(id+"F0.imprint","IMPRINT",FACE,{"disambiguationData":[TD([[makeQuery(id+"F0.imprint","IMPRINT",EDGE,{"disambiguationData":[TD([[subQ2,-1.0]])],"derivedFrom":subQ1}),1.0]])]});}
            var Q69;
            {var subQ5=sQuery(id+"F0.wireOp",EDGE,"E16.bottom");Q69=makeQuery(id+"F0.imprint","IMPRINT",FACE,{"disambiguationData":[TD([[makeQuery(id+"F0.imprint","IMPRINT",EDGE,{"derivedFrom":subQ5}),-1.0]])]});}
            var Q70;
            {var subQ5=sQuery(id+"F0.wireOp",EDGE,"E18.top");Q70=makeQuery(id+"F0.imprint","IMPRINT",FACE,{"disambiguationData":[TD([[makeQuery(id+"F0.imprint","IMPRINT",EDGE,{"derivedFrom":subQ5}),1.0]])]});}
            var Q71;
            {var subQ0=sQuery(id+"F0.wireOp",EDGE,"E18.right");var subQ1=sQuery(id+"F0.wireOp",EDGE,"E0");var subQ2=makeQuery(id+"F0.imprint","INTERSECT",VERTEX,{"disambiguationData":[OD(0.0)],"derivedFrom":[subQ1,subQ0]});Q71=makeQuery(id+"F0.imprint","IMPRINT",FACE,{"disambiguationData":[TD([[makeQuery(id+"F0.imprint","IMPRINT",EDGE,{"disambiguationData":[TD([[subQ2,-1.0]])],"derivedFrom":subQ1}),-1.0]])]});}
            var Q72;
            {var subQ5=sQuery(id+"F0.wireOp",EDGE,"E17.top");Q72=makeQuery(id+"F0.imprint","IMPRINT",FACE,{"disambiguationData":[TD([[makeQuery(id+"F0.imprint","IMPRINT",EDGE,{"derivedFrom":subQ5}),1.0]])]});}
            var Q73;
            {var subQ0=sQuery(id+"F0.wireOp",EDGE,"E17.right");var subQ1=sQuery(id+"F0.wireOp",EDGE,"E0");var subQ2=makeQuery(id+"F0.imprint","INTERSECT",VERTEX,{"disambiguationData":[OD(0.0)],"derivedFrom":[subQ1,subQ0]});Q73=makeQuery(id+"F0.imprint","IMPRINT",FACE,{"disambiguationData":[TD([[makeQuery(id+"F0.imprint","IMPRINT",EDGE,{"disambiguationData":[TD([[subQ2,-1.0]])],"derivedFrom":subQ1}),-1.0]])]});}
            var Q74;
            {var subQ0=sQuery(id+"F0.wireOp",EDGE,"E16.right");var subQ1=sQuery(id+"F0.wireOp",EDGE,"E0");var subQ2=makeQuery(id+"F0.imprint","INTERSECT",VERTEX,{"disambiguationData":[OD(0.0)],"derivedFrom":[subQ1,subQ0]});Q74=makeQuery(id+"F0.imprint","IMPRINT",FACE,{"disambiguationData":[TD([[makeQuery(id+"F0.imprint","IMPRINT",EDGE,{"disambiguationData":[TD([[subQ2,-1.0]])],"derivedFrom":subQ1}),1.0]])]});}
            var Q75;
            {var subQ5=sQuery(id+"F0.wireOp",EDGE,"E15.top");Q75=makeQuery(id+"F0.imprint","IMPRINT",FACE,{"disambiguationData":[TD([[makeQuery(id+"F0.imprint","IMPRINT",EDGE,{"derivedFrom":subQ5}),1.0]])]});}
            var Q76;
            {var subQ0=sQuery(id+"F0.wireOp",EDGE,"E15.left");var subQ1=sQuery(id+"F0.wireOp",EDGE,"E0");var subQ2=makeQuery(id+"F0.imprint","INTERSECT",VERTEX,{"disambiguationData":[OD(1.0)],"derivedFrom":[subQ1,subQ0]});Q76=makeQuery(id+"F0.imprint","IMPRINT",FACE,{"disambiguationData":[TD([[makeQuery(id+"F0.imprint","IMPRINT",EDGE,{"disambiguationData":[TD([[subQ2,-1.0]])],"derivedFrom":subQ1}),1.0]])]});}
            var Q77;
            {var subQ0=sQuery(id+"F0.wireOp",EDGE,"E12.right");var subQ1=sQuery(id+"F0.wireOp",EDGE,"E0");var subQ2=makeQuery(id+"F0.imprint","INTERSECT",VERTEX,{"disambiguationData":[OD(1.0)],"derivedFrom":[subQ1,subQ0]});Q77=makeQuery(id+"F0.imprint","IMPRINT",FACE,{"disambiguationData":[TD([[makeQuery(id+"F0.imprint","IMPRINT",EDGE,{"disambiguationData":[TD([[subQ2,-1.0]])],"derivedFrom":subQ1}),1.0]])]});}
            var Q78;
            {var subQ0=sQuery(id+"F0.wireOp",EDGE,"E13.left");var subQ1=sQuery(id+"F0.wireOp",EDGE,"E0");var subQ2=makeQuery(id+"F0.imprint","INTERSECT",VERTEX,{"disambiguationData":[OD(1.0)],"derivedFrom":[subQ1,subQ0]});Q78=makeQuery(id+"F0.imprint","IMPRINT",FACE,{"disambiguationData":[TD([[makeQuery(id+"F0.imprint","IMPRINT",EDGE,{"disambiguationData":[TD([[subQ2,-1.0]])],"derivedFrom":subQ1}),1.0]])]});}
            var Q79;
            {var subQ5=sQuery(id+"F0.wireOp",EDGE,"E14.bottom");Q79=makeQuery(id+"F0.imprint","IMPRINT",FACE,{"disambiguationData":[TD([[makeQuery(id+"F0.imprint","IMPRINT",EDGE,{"derivedFrom":subQ5}),-1.0]])]});}
            var Q80;
            {var subQ0=sQuery(id+"F0.wireOp",EDGE,"E15.right");var subQ1=sQuery(id+"F0.wireOp",EDGE,"E0");var subQ2=makeQuery(id+"F0.imprint","INTERSECT",VERTEX,{"disambiguationData":[OD(1.0)],"derivedFrom":[subQ1,subQ0]});Q80=makeQuery(id+"F0.imprint","IMPRINT",FACE,{"disambiguationData":[TD([[makeQuery(id+"F0.imprint","IMPRINT",EDGE,{"disambiguationData":[TD([[subQ2,-1.0]])],"derivedFrom":subQ1}),-1.0]])]});}
            var Q81;
            {var subQ0=sQuery(id+"F0.wireOp",EDGE,"E14.right");var subQ1=sQuery(id+"F0.wireOp",EDGE,"E0");var subQ2=makeQuery(id+"F0.imprint","INTERSECT",VERTEX,{"disambiguationData":[OD(1.0)],"derivedFrom":[subQ1,subQ0]});Q81=makeQuery(id+"F0.imprint","IMPRINT",FACE,{"disambiguationData":[TD([[makeQuery(id+"F0.imprint","IMPRINT",EDGE,{"disambiguationData":[TD([[subQ2,-1.0]])],"derivedFrom":subQ1}),1.0]])]});}
            var Q82;
            {var subQ0=sQuery(id+"F0.wireOp",EDGE,"E22.left");var subQ1=sQuery(id+"F0.wireOp",EDGE,"E0");var subQ2=makeQuery(id+"F0.imprint","INTERSECT",VERTEX,{"disambiguationData":[OD(1.0)],"derivedFrom":[subQ1,subQ0]});Q82=makeQuery(id+"F0.imprint","IMPRINT",FACE,{"disambiguationData":[TD([[makeQuery(id+"F0.imprint","IMPRINT",EDGE,{"disambiguationData":[TD([[subQ2,-1.0]])],"derivedFrom":subQ1}),1.0]])]});}
            var Q83;
            {var subQ0=sQuery(id+"F0.wireOp",EDGE,"E21.left");var subQ1=sQuery(id+"F0.wireOp",EDGE,"E0");var subQ2=makeQuery(id+"F0.imprint","INTERSECT",VERTEX,{"disambiguationData":[OD(1.0)],"derivedFrom":[subQ1,subQ0]});Q83=makeQuery(id+"F0.imprint","IMPRINT",FACE,{"disambiguationData":[TD([[makeQuery(id+"F0.imprint","IMPRINT",EDGE,{"disambiguationData":[TD([[subQ2,-1.0]])],"derivedFrom":subQ1}),1.0]])]});}
            var Q84;
            {var subQ0=sQuery(id+"F0.wireOp",EDGE,"E20.left");var subQ1=sQuery(id+"F0.wireOp",EDGE,"E0");var subQ2=makeQuery(id+"F0.imprint","INTERSECT",VERTEX,{"disambiguationData":[OD(1.0)],"derivedFrom":[subQ1,subQ0]});Q84=makeQuery(id+"F0.imprint","IMPRINT",FACE,{"disambiguationData":[TD([[makeQuery(id+"F0.imprint","IMPRINT",EDGE,{"disambiguationData":[TD([[subQ2,-1.0]])],"derivedFrom":subQ1}),1.0]])]});}
            var Q85;
            {var subQ0=sQuery(id+"F0.wireOp",EDGE,"E19.left");var subQ1=sQuery(id+"F0.wireOp",EDGE,"E0");var subQ2=makeQuery(id+"F0.imprint","INTERSECT",VERTEX,{"disambiguationData":[OD(1.0)],"derivedFrom":[subQ1,subQ0]});Q85=makeQuery(id+"F0.imprint","IMPRINT",FACE,{"disambiguationData":[TD([[makeQuery(id+"F0.imprint","IMPRINT",EDGE,{"disambiguationData":[TD([[subQ2,-1.0]])],"derivedFrom":subQ1}),1.0]])]});}
            var Q86;
            {var subQ0=sQuery(id+"F0.wireOp",EDGE,"E18.right");var subQ1=sQuery(id+"F0.wireOp",EDGE,"E0");var subQ2=makeQuery(id+"F0.imprint","INTERSECT",VERTEX,{"disambiguationData":[OD(1.0)],"derivedFrom":[subQ1,subQ0]});Q86=makeQuery(id+"F0.imprint","IMPRINT",FACE,{"disambiguationData":[TD([[makeQuery(id+"F0.imprint","IMPRINT",EDGE,{"disambiguationData":[TD([[subQ2,-1.0]])],"derivedFrom":subQ1}),1.0]])]});}
            var Q87;
            {var subQ0=sQuery(id+"F0.wireOp",EDGE,"E17.right");var subQ1=sQuery(id+"F0.wireOp",EDGE,"E0");var subQ2=makeQuery(id+"F0.imprint","INTERSECT",VERTEX,{"disambiguationData":[OD(1.0)],"derivedFrom":[subQ1,subQ0]});Q87=makeQuery(id+"F0.imprint","IMPRINT",FACE,{"disambiguationData":[TD([[makeQuery(id+"F0.imprint","IMPRINT",EDGE,{"disambiguationData":[TD([[subQ2,-1.0]])],"derivedFrom":subQ1}),1.0]])]});}
            extrude(context, id + "F1", {"entities" : qUnion([Q0, Q1, Q2, Q3, Q4, Q5, Q6, Q7, Q8, Q9, Q10, Q11, Q12, Q13, Q14, Q15, Q16, Q17, Q18, Q19, Q20, Q21, Q22, Q23, Q24, Q25, Q26, Q27, Q28, Q29, Q30, Q31, Q32, Q33, Q34, Q35, Q36, Q37, Q38, Q39, Q40, Q41, Q42, Q43, Q44, Q45, Q46, Q47, Q48, Q49, Q50, Q51, Q52, Q53, Q54, Q55, Q56, Q57, Q58, Q59, Q60, Q61, Q62, Q63, Q64, Q65, Q66, Q67, Q68, Q69, Q70, Q71, Q72, Q73, Q74, Q75, Q76, Q77, Q78, Q79, Q80, Q81, Q82, Q83, Q84, Q85, Q86, Q87]), "depth" : 10 * mm, "offsetDistance" : 25 * mm});
        }
        {
            var Q0;
            Q0=makeQuery(id+"F0.imprint","IMPRINT",FACE,{"disambiguationData":[TD([[makeQuery(id+"F0.imprint","IMPRINT",EDGE,{"derivedFrom":sQuery(id+"F0.wireOp",EDGE,"E5")}),1.0]])]});
            extrude(context, id + "F2", {"entities" : qUnion([Q0]), "depth" : 9 * mm, "offsetDistance" : 25 * mm});
        }
        {
            var Q0;
            {var subQ0=sQuery(id+"F0.wireOp",EDGE,"E11.right");var subQ1=sQuery(id+"F0.wireOp",EDGE,"E0");Q0=makeQuery(id+"F1.opExtrude","SWEPT_EDGE",EDGE,{"disambiguationData":[OSD([subQ1,subQ0]),TDD([makeQuery(id+"F0.imprint","INTERSECT",VERTEX,{"disambiguationData":[OD(0.0)],"derivedFrom":[subQ1,subQ0]})])]});}
            var Q1;
            {var subQ0=sQuery(id+"F0.wireOp",EDGE,"E10.left");var subQ1=sQuery(id+"F0.wireOp",EDGE,"E0");Q1=makeQuery(id+"F1.opExtrude","SWEPT_EDGE",EDGE,{"disambiguationData":[OSD([subQ1,subQ0]),TDD([makeQuery(id+"F0.imprint","INTERSECT",VERTEX,{"disambiguationData":[OD(0.0)],"derivedFrom":[subQ1,subQ0]})])]});}
            var Q2;
            {var subQ0=sQuery(id+"F0.wireOp",EDGE,"E9.bottom");var subQ1=sQuery(id+"F0.wireOp",EDGE,"E0");Q2=makeQuery(id+"F1.opExtrude","SWEPT_EDGE",EDGE,{"disambiguationData":[OSD([subQ1,subQ0]),TDD([makeQuery(id+"F0.imprint","INTERSECT",VERTEX,{"disambiguationData":[OD(0.0)],"derivedFrom":[subQ1,subQ0]})])]});}
            var Q3;
            {var subQ0=sQuery(id+"F0.wireOp",EDGE,"E8.left");var subQ1=sQuery(id+"F0.wireOp",EDGE,"E0");Q3=makeQuery(id+"F1.opExtrude","SWEPT_EDGE",EDGE,{"disambiguationData":[OSD([subQ1,subQ0]),TDD([makeQuery(id+"F0.imprint","INTERSECT",VERTEX,{"disambiguationData":[OD(0.0)],"derivedFrom":[subQ1,subQ0]})])]});}
            var Q4;
            {var subQ0=sQuery(id+"F0.wireOp",EDGE,"E8.right");var subQ1=sQuery(id+"F0.wireOp",EDGE,"E0");Q4=makeQuery(id+"F1.opExtrude","SWEPT_EDGE",EDGE,{"disambiguationData":[OSD([subQ1,subQ0]),TDD([makeQuery(id+"F0.imprint","INTERSECT",VERTEX,{"disambiguationData":[OD(0.0)],"derivedFrom":[subQ1,subQ0]})])]});}
            var Q5;
            {var subQ0=sQuery(id+"F0.wireOp",EDGE,"E9.top");var subQ1=sQuery(id+"F0.wireOp",EDGE,"E0");Q5=makeQuery(id+"F1.opExtrude","SWEPT_EDGE",EDGE,{"disambiguationData":[OSD([subQ1,subQ0]),TDD([makeQuery(id+"F0.imprint","INTERSECT",VERTEX,{"disambiguationData":[OD(0.0)],"derivedFrom":[subQ1,subQ0]})])]});}
            var Q6;
            {var subQ0=sQuery(id+"F0.wireOp",EDGE,"E10.right");var subQ1=sQuery(id+"F0.wireOp",EDGE,"E0");Q6=makeQuery(id+"F1.opExtrude","SWEPT_EDGE",EDGE,{"disambiguationData":[OSD([subQ1,subQ0]),TDD([makeQuery(id+"F0.imprint","INTERSECT",VERTEX,{"disambiguationData":[OD(0.0)],"derivedFrom":[subQ1,subQ0]})])]});}
            var Q7;
            {var subQ0=sQuery(id+"F0.wireOp",EDGE,"E11.left");var subQ1=sQuery(id+"F0.wireOp",EDGE,"E0");Q7=makeQuery(id+"F1.opExtrude","SWEPT_EDGE",EDGE,{"disambiguationData":[OSD([subQ1,subQ0]),TDD([makeQuery(id+"F0.imprint","INTERSECT",VERTEX,{"disambiguationData":[OD(0.0)],"derivedFrom":[subQ1,subQ0]})])]});}
            var Q8;
            {var subQ0=sQuery(id+"F0.wireOp",EDGE,"E10.left");var subQ1=sQuery(id+"F0.wireOp",EDGE,"E0");Q8=makeQuery(id+"F1.opExtrude","SWEPT_EDGE",EDGE,{"disambiguationData":[OSD([subQ1,subQ0]),TDD([makeQuery(id+"F0.imprint","INTERSECT",VERTEX,{"disambiguationData":[OD(1.0)],"derivedFrom":[subQ1,subQ0]})])]});}
            var Q9;
            {var subQ0=sQuery(id+"F0.wireOp",EDGE,"E11.right");var subQ1=sQuery(id+"F0.wireOp",EDGE,"E0");Q9=makeQuery(id+"F1.opExtrude","SWEPT_EDGE",EDGE,{"disambiguationData":[OSD([subQ1,subQ0]),TDD([makeQuery(id+"F0.imprint","INTERSECT",VERTEX,{"disambiguationData":[OD(1.0)],"derivedFrom":[subQ1,subQ0]})])]});}
            var Q10;
            {var subQ0=sQuery(id+"F0.wireOp",EDGE,"E8.right");var subQ1=sQuery(id+"F0.wireOp",EDGE,"E0");Q10=makeQuery(id+"F1.opExtrude","SWEPT_EDGE",EDGE,{"disambiguationData":[OSD([subQ1,subQ0]),TDD([makeQuery(id+"F0.imprint","INTERSECT",VERTEX,{"disambiguationData":[OD(1.0)],"derivedFrom":[subQ1,subQ0]})])]});}
            var Q11;
            {var subQ0=sQuery(id+"F0.wireOp",EDGE,"E9.top");var subQ1=sQuery(id+"F0.wireOp",EDGE,"E0");Q11=makeQuery(id+"F1.opExtrude","SWEPT_EDGE",EDGE,{"disambiguationData":[OSD([subQ1,subQ0]),TDD([makeQuery(id+"F0.imprint","INTERSECT",VERTEX,{"disambiguationData":[OD(1.0)],"derivedFrom":[subQ1,subQ0]})])]});}
            var Q12;
            {var subQ0=sQuery(id+"F0.wireOp",EDGE,"E10.right");var subQ1=sQuery(id+"F0.wireOp",EDGE,"E0");Q12=makeQuery(id+"F1.opExtrude","SWEPT_EDGE",EDGE,{"disambiguationData":[OSD([subQ1,subQ0]),TDD([makeQuery(id+"F0.imprint","INTERSECT",VERTEX,{"disambiguationData":[OD(1.0)],"derivedFrom":[subQ1,subQ0]})])]});}
            var Q13;
            {var subQ0=sQuery(id+"F0.wireOp",EDGE,"E11.left");var subQ1=sQuery(id+"F0.wireOp",EDGE,"E0");Q13=makeQuery(id+"F1.opExtrude","SWEPT_EDGE",EDGE,{"disambiguationData":[OSD([subQ1,subQ0]),TDD([makeQuery(id+"F0.imprint","INTERSECT",VERTEX,{"disambiguationData":[OD(1.0)],"derivedFrom":[subQ1,subQ0]})])]});}
            var Q14;
            {var subQ0=sQuery(id+"F0.wireOp",EDGE,"E8.left");var subQ1=sQuery(id+"F0.wireOp",EDGE,"E0");Q14=makeQuery(id+"F1.opExtrude","SWEPT_EDGE",EDGE,{"disambiguationData":[OSD([subQ1,subQ0]),TDD([makeQuery(id+"F0.imprint","INTERSECT",VERTEX,{"disambiguationData":[OD(1.0)],"derivedFrom":[subQ1,subQ0]})])]});}
            var Q15;
            {var subQ0=sQuery(id+"F0.wireOp",EDGE,"E9.bottom");var subQ1=sQuery(id+"F0.wireOp",EDGE,"E0");Q15=makeQuery(id+"F1.opExtrude","SWEPT_EDGE",EDGE,{"disambiguationData":[OSD([subQ1,subQ0]),TDD([makeQuery(id+"F0.imprint","INTERSECT",VERTEX,{"disambiguationData":[OD(1.0)],"derivedFrom":[subQ1,subQ0]})])]});}
            var Q16;
            {var subQ0=sQuery(id+"F0.wireOp",EDGE,"E22.left");var subQ1=sQuery(id+"F0.wireOp",EDGE,"E0");Q16=makeQuery(id+"F1.opExtrude","SWEPT_EDGE",EDGE,{"disambiguationData":[OSD([subQ1,subQ0]),TDD([makeQuery(id+"F0.imprint","INTERSECT",VERTEX,{"disambiguationData":[OD(0.0)],"derivedFrom":[subQ1,subQ0]})])]});}
            var Q17;
            {var subQ0=sQuery(id+"F0.wireOp",EDGE,"E21.left");var subQ1=sQuery(id+"F0.wireOp",EDGE,"E0");Q17=makeQuery(id+"F1.opExtrude","SWEPT_EDGE",EDGE,{"disambiguationData":[OSD([subQ1,subQ0]),TDD([makeQuery(id+"F0.imprint","INTERSECT",VERTEX,{"disambiguationData":[OD(0.0)],"derivedFrom":[subQ1,subQ0]})])]});}
            var Q18;
            {var subQ0=sQuery(id+"F0.wireOp",EDGE,"E20.left");var subQ1=sQuery(id+"F0.wireOp",EDGE,"E0");Q18=makeQuery(id+"F1.opExtrude","SWEPT_EDGE",EDGE,{"disambiguationData":[OSD([subQ1,subQ0]),TDD([makeQuery(id+"F0.imprint","INTERSECT",VERTEX,{"disambiguationData":[OD(0.0)],"derivedFrom":[subQ1,subQ0]})])]});}
            var Q19;
            {var subQ0=sQuery(id+"F0.wireOp",EDGE,"E19.left");var subQ1=sQuery(id+"F0.wireOp",EDGE,"E0");Q19=makeQuery(id+"F1.opExtrude","SWEPT_EDGE",EDGE,{"disambiguationData":[OSD([subQ1,subQ0]),TDD([makeQuery(id+"F0.imprint","INTERSECT",VERTEX,{"disambiguationData":[OD(0.0)],"derivedFrom":[subQ1,subQ0]})])]});}
            var Q20;
            {var subQ0=sQuery(id+"F0.wireOp",EDGE,"E18.right");var subQ1=sQuery(id+"F0.wireOp",EDGE,"E0");Q20=makeQuery(id+"F1.opExtrude","SWEPT_EDGE",EDGE,{"disambiguationData":[OSD([subQ1,subQ0]),TDD([makeQuery(id+"F0.imprint","INTERSECT",VERTEX,{"disambiguationData":[OD(0.0)],"derivedFrom":[subQ1,subQ0]})])]});}
            var Q21;
            {var subQ0=sQuery(id+"F0.wireOp",EDGE,"E17.right");var subQ1=sQuery(id+"F0.wireOp",EDGE,"E0");Q21=makeQuery(id+"F1.opExtrude","SWEPT_EDGE",EDGE,{"disambiguationData":[OSD([subQ1,subQ0]),TDD([makeQuery(id+"F0.imprint","INTERSECT",VERTEX,{"disambiguationData":[OD(0.0)],"derivedFrom":[subQ1,subQ0]})])]});}
            var Q22;
            {var subQ0=sQuery(id+"F0.wireOp",EDGE,"E12.left");var subQ1=sQuery(id+"F0.wireOp",EDGE,"E0");Q22=makeQuery(id+"F1.opExtrude","SWEPT_EDGE",EDGE,{"disambiguationData":[OSD([subQ1,subQ0]),TDD([makeQuery(id+"F0.imprint","INTERSECT",VERTEX,{"disambiguationData":[OD(0.0)],"derivedFrom":[subQ1,subQ0]})])]});}
            var Q23;
            {var subQ0=sQuery(id+"F0.wireOp",EDGE,"E13.right");var subQ1=sQuery(id+"F0.wireOp",EDGE,"E0");Q23=makeQuery(id+"F1.opExtrude","SWEPT_EDGE",EDGE,{"disambiguationData":[OSD([subQ1,subQ0]),TDD([makeQuery(id+"F0.imprint","INTERSECT",VERTEX,{"disambiguationData":[OD(0.0)],"derivedFrom":[subQ1,subQ0]})])]});}
            var Q24;
            {var subQ0=sQuery(id+"F0.wireOp",EDGE,"E14.left");var subQ1=sQuery(id+"F0.wireOp",EDGE,"E0");Q24=makeQuery(id+"F1.opExtrude","SWEPT_EDGE",EDGE,{"disambiguationData":[OSD([subQ1,subQ0]),TDD([makeQuery(id+"F0.imprint","INTERSECT",VERTEX,{"disambiguationData":[OD(0.0)],"derivedFrom":[subQ1,subQ0]})])]});}
            var Q25;
            {var subQ0=sQuery(id+"F0.wireOp",EDGE,"E15.left");var subQ1=sQuery(id+"F0.wireOp",EDGE,"E0");Q25=makeQuery(id+"F1.opExtrude","SWEPT_EDGE",EDGE,{"disambiguationData":[OSD([subQ1,subQ0]),TDD([makeQuery(id+"F0.imprint","INTERSECT",VERTEX,{"disambiguationData":[OD(0.0)],"derivedFrom":[subQ1,subQ0]})])]});}
            var Q26;
            {var subQ0=sQuery(id+"F0.wireOp",EDGE,"E16.right");var subQ1=sQuery(id+"F0.wireOp",EDGE,"E0");Q26=makeQuery(id+"F1.opExtrude","SWEPT_EDGE",EDGE,{"disambiguationData":[OSD([subQ1,subQ0]),TDD([makeQuery(id+"F0.imprint","INTERSECT",VERTEX,{"disambiguationData":[OD(1.0)],"derivedFrom":[subQ1,subQ0]})])]});}
            var Q27;
            {var subQ0=sQuery(id+"F0.wireOp",EDGE,"E17.left");var subQ1=sQuery(id+"F0.wireOp",EDGE,"E0");Q27=makeQuery(id+"F1.opExtrude","SWEPT_EDGE",EDGE,{"disambiguationData":[OSD([subQ1,subQ0]),TDD([makeQuery(id+"F0.imprint","INTERSECT",VERTEX,{"disambiguationData":[OD(1.0)],"derivedFrom":[subQ1,subQ0]})])]});}
            var Q28;
            {var subQ0=sQuery(id+"F0.wireOp",EDGE,"E18.left");var subQ1=sQuery(id+"F0.wireOp",EDGE,"E0");Q28=makeQuery(id+"F1.opExtrude","SWEPT_EDGE",EDGE,{"disambiguationData":[OSD([subQ1,subQ0]),TDD([makeQuery(id+"F0.imprint","INTERSECT",VERTEX,{"disambiguationData":[OD(1.0)],"derivedFrom":[subQ1,subQ0]})])]});}
            var Q29;
            {var subQ0=sQuery(id+"F0.wireOp",EDGE,"E19.right");var subQ1=sQuery(id+"F0.wireOp",EDGE,"E0");Q29=makeQuery(id+"F1.opExtrude","SWEPT_EDGE",EDGE,{"disambiguationData":[OSD([subQ1,subQ0]),TDD([makeQuery(id+"F0.imprint","INTERSECT",VERTEX,{"disambiguationData":[OD(1.0)],"derivedFrom":[subQ1,subQ0]})])]});}
            var Q30;
            {var subQ0=sQuery(id+"F0.wireOp",EDGE,"E21.left");var subQ1=sQuery(id+"F0.wireOp",EDGE,"E0");Q30=makeQuery(id+"F1.opExtrude","SWEPT_EDGE",EDGE,{"disambiguationData":[OSD([subQ1,subQ0]),TDD([makeQuery(id+"F0.imprint","INTERSECT",VERTEX,{"disambiguationData":[OD(1.0)],"derivedFrom":[subQ1,subQ0]})])]});}
            var Q31;
            {var subQ0=sQuery(id+"F0.wireOp",EDGE,"E22.left");var subQ1=sQuery(id+"F0.wireOp",EDGE,"E0");Q31=makeQuery(id+"F1.opExtrude","SWEPT_EDGE",EDGE,{"disambiguationData":[OSD([subQ1,subQ0]),TDD([makeQuery(id+"F0.imprint","INTERSECT",VERTEX,{"disambiguationData":[OD(1.0)],"derivedFrom":[subQ1,subQ0]})])]});}
            var Q32;
            {var subQ0=sQuery(id+"F0.wireOp",EDGE,"E12.right");var subQ1=sQuery(id+"F0.wireOp",EDGE,"E0");Q32=makeQuery(id+"F1.opExtrude","SWEPT_EDGE",EDGE,{"disambiguationData":[OSD([subQ1,subQ0]),TDD([makeQuery(id+"F0.imprint","INTERSECT",VERTEX,{"disambiguationData":[OD(1.0)],"derivedFrom":[subQ1,subQ0]})])]});}
            var Q33;
            {var subQ0=sQuery(id+"F0.wireOp",EDGE,"E20.right");var subQ1=sQuery(id+"F0.wireOp",EDGE,"E0");Q33=makeQuery(id+"F1.opExtrude","SWEPT_EDGE",EDGE,{"disambiguationData":[OSD([subQ1,subQ0]),TDD([makeQuery(id+"F0.imprint","INTERSECT",VERTEX,{"disambiguationData":[OD(1.0)],"derivedFrom":[subQ1,subQ0]})])]});}
            var Q34;
            {var subQ0=sQuery(id+"F0.wireOp",EDGE,"E13.left");var subQ1=sQuery(id+"F0.wireOp",EDGE,"E0");Q34=makeQuery(id+"F1.opExtrude","SWEPT_EDGE",EDGE,{"disambiguationData":[OSD([subQ1,subQ0]),TDD([makeQuery(id+"F0.imprint","INTERSECT",VERTEX,{"disambiguationData":[OD(1.0)],"derivedFrom":[subQ1,subQ0]})])]});}
            var Q35;
            {var subQ0=sQuery(id+"F0.wireOp",EDGE,"E14.right");var subQ1=sQuery(id+"F0.wireOp",EDGE,"E0");Q35=makeQuery(id+"F1.opExtrude","SWEPT_EDGE",EDGE,{"disambiguationData":[OSD([subQ1,subQ0]),TDD([makeQuery(id+"F0.imprint","INTERSECT",VERTEX,{"disambiguationData":[OD(1.0)],"derivedFrom":[subQ1,subQ0]})])]});}
            var Q36;
            {var subQ0=sQuery(id+"F0.wireOp",EDGE,"E21.right");var subQ1=sQuery(id+"F0.wireOp",EDGE,"E0");Q36=makeQuery(id+"F1.opExtrude","SWEPT_EDGE",EDGE,{"disambiguationData":[OSD([subQ1,subQ0]),TDD([makeQuery(id+"F0.imprint","INTERSECT",VERTEX,{"disambiguationData":[OD(1.0)],"derivedFrom":[subQ1,subQ0]})])]});}
            var Q37;
            {var subQ0=sQuery(id+"F0.wireOp",EDGE,"E22.right");var subQ1=sQuery(id+"F0.wireOp",EDGE,"E0");Q37=makeQuery(id+"F1.opExtrude","SWEPT_EDGE",EDGE,{"disambiguationData":[OSD([subQ1,subQ0]),TDD([makeQuery(id+"F0.imprint","INTERSECT",VERTEX,{"disambiguationData":[OD(1.0)],"derivedFrom":[subQ1,subQ0]})])]});}
            var Q38;
            {var subQ0=sQuery(id+"F0.wireOp",EDGE,"E22.right");var subQ1=sQuery(id+"F0.wireOp",EDGE,"E0");Q38=makeQuery(id+"F1.opExtrude","SWEPT_EDGE",EDGE,{"disambiguationData":[OSD([subQ1,subQ0]),TDD([makeQuery(id+"F0.imprint","INTERSECT",VERTEX,{"disambiguationData":[OD(0.0)],"derivedFrom":[subQ1,subQ0]})])]});}
            var Q39;
            {var subQ0=sQuery(id+"F0.wireOp",EDGE,"E21.right");var subQ1=sQuery(id+"F0.wireOp",EDGE,"E0");Q39=makeQuery(id+"F1.opExtrude","SWEPT_EDGE",EDGE,{"disambiguationData":[OSD([subQ1,subQ0]),TDD([makeQuery(id+"F0.imprint","INTERSECT",VERTEX,{"disambiguationData":[OD(0.0)],"derivedFrom":[subQ1,subQ0]})])]});}
            var Q40;
            {var subQ0=sQuery(id+"F0.wireOp",EDGE,"E20.right");var subQ1=sQuery(id+"F0.wireOp",EDGE,"E0");Q40=makeQuery(id+"F1.opExtrude","SWEPT_EDGE",EDGE,{"disambiguationData":[OSD([subQ1,subQ0]),TDD([makeQuery(id+"F0.imprint","INTERSECT",VERTEX,{"disambiguationData":[OD(0.0)],"derivedFrom":[subQ1,subQ0]})])]});}
            var Q41;
            {var subQ0=sQuery(id+"F0.wireOp",EDGE,"E15.right");var subQ1=sQuery(id+"F0.wireOp",EDGE,"E0");Q41=makeQuery(id+"F1.opExtrude","SWEPT_EDGE",EDGE,{"disambiguationData":[OSD([subQ1,subQ0]),TDD([makeQuery(id+"F0.imprint","INTERSECT",VERTEX,{"disambiguationData":[OD(1.0)],"derivedFrom":[subQ1,subQ0]})])]});}
            var Q42;
            {var subQ0=sQuery(id+"F0.wireOp",EDGE,"E16.left");var subQ1=sQuery(id+"F0.wireOp",EDGE,"E0");Q42=makeQuery(id+"F1.opExtrude","SWEPT_EDGE",EDGE,{"disambiguationData":[OSD([subQ1,subQ0]),TDD([makeQuery(id+"F0.imprint","INTERSECT",VERTEX,{"disambiguationData":[OD(0.0)],"derivedFrom":[subQ1,subQ0]})])]});}
            var Q43;
            {var subQ0=sQuery(id+"F0.wireOp",EDGE,"E14.left");var subQ1=sQuery(id+"F0.wireOp",EDGE,"E0");Q43=makeQuery(id+"F1.opExtrude","SWEPT_EDGE",EDGE,{"disambiguationData":[OSD([subQ1,subQ0]),TDD([makeQuery(id+"F0.imprint","INTERSECT",VERTEX,{"disambiguationData":[OD(1.0)],"derivedFrom":[subQ1,subQ0]})])]});}
            var Q44;
            {var subQ0=sQuery(id+"F0.wireOp",EDGE,"E19.right");var subQ1=sQuery(id+"F0.wireOp",EDGE,"E0");Q44=makeQuery(id+"F1.opExtrude","SWEPT_EDGE",EDGE,{"disambiguationData":[OSD([subQ1,subQ0]),TDD([makeQuery(id+"F0.imprint","INTERSECT",VERTEX,{"disambiguationData":[OD(0.0)],"derivedFrom":[subQ1,subQ0]})])]});}
            var Q45;
            {var subQ0=sQuery(id+"F0.wireOp",EDGE,"E18.left");var subQ1=sQuery(id+"F0.wireOp",EDGE,"E0");Q45=makeQuery(id+"F1.opExtrude","SWEPT_EDGE",EDGE,{"disambiguationData":[OSD([subQ1,subQ0]),TDD([makeQuery(id+"F0.imprint","INTERSECT",VERTEX,{"disambiguationData":[OD(0.0)],"derivedFrom":[subQ1,subQ0]})])]});}
            var Q46;
            {var subQ0=sQuery(id+"F0.wireOp",EDGE,"E15.left");var subQ1=sQuery(id+"F0.wireOp",EDGE,"E0");Q46=makeQuery(id+"F1.opExtrude","SWEPT_EDGE",EDGE,{"disambiguationData":[OSD([subQ1,subQ0]),TDD([makeQuery(id+"F0.imprint","INTERSECT",VERTEX,{"disambiguationData":[OD(1.0)],"derivedFrom":[subQ1,subQ0]})])]});}
            var Q47;
            {var subQ0=sQuery(id+"F0.wireOp",EDGE,"E16.right");var subQ1=sQuery(id+"F0.wireOp",EDGE,"E0");Q47=makeQuery(id+"F1.opExtrude","SWEPT_EDGE",EDGE,{"disambiguationData":[OSD([subQ1,subQ0]),TDD([makeQuery(id+"F0.imprint","INTERSECT",VERTEX,{"disambiguationData":[OD(0.0)],"derivedFrom":[subQ1,subQ0]})])]});}
            var Q48;
            {var subQ0=sQuery(id+"F0.wireOp",EDGE,"E12.left");var subQ1=sQuery(id+"F0.wireOp",EDGE,"E0");Q48=makeQuery(id+"F1.opExtrude","SWEPT_EDGE",EDGE,{"disambiguationData":[OSD([subQ1,subQ0]),TDD([makeQuery(id+"F0.imprint","INTERSECT",VERTEX,{"disambiguationData":[OD(1.0)],"derivedFrom":[subQ1,subQ0]})])]});}
            var Q49;
            {var subQ0=sQuery(id+"F0.wireOp",EDGE,"E13.right");var subQ1=sQuery(id+"F0.wireOp",EDGE,"E0");Q49=makeQuery(id+"F1.opExtrude","SWEPT_EDGE",EDGE,{"disambiguationData":[OSD([subQ1,subQ0]),TDD([makeQuery(id+"F0.imprint","INTERSECT",VERTEX,{"disambiguationData":[OD(1.0)],"derivedFrom":[subQ1,subQ0]})])]});}
            var Q50;
            {var subQ0=sQuery(id+"F0.wireOp",EDGE,"E19.left");var subQ1=sQuery(id+"F0.wireOp",EDGE,"E0");Q50=makeQuery(id+"F1.opExtrude","SWEPT_EDGE",EDGE,{"disambiguationData":[OSD([subQ1,subQ0]),TDD([makeQuery(id+"F0.imprint","INTERSECT",VERTEX,{"disambiguationData":[OD(1.0)],"derivedFrom":[subQ1,subQ0]})])]});}
            var Q51;
            {var subQ0=sQuery(id+"F0.wireOp",EDGE,"E17.right");var subQ1=sQuery(id+"F0.wireOp",EDGE,"E0");Q51=makeQuery(id+"F1.opExtrude","SWEPT_EDGE",EDGE,{"disambiguationData":[OSD([subQ1,subQ0]),TDD([makeQuery(id+"F0.imprint","INTERSECT",VERTEX,{"disambiguationData":[OD(1.0)],"derivedFrom":[subQ1,subQ0]})])]});}
            var Q52;
            {var subQ0=sQuery(id+"F0.wireOp",EDGE,"E13.left");var subQ1=sQuery(id+"F0.wireOp",EDGE,"E0");Q52=makeQuery(id+"F1.opExtrude","SWEPT_EDGE",EDGE,{"disambiguationData":[OSD([subQ1,subQ0]),TDD([makeQuery(id+"F0.imprint","INTERSECT",VERTEX,{"disambiguationData":[OD(0.0)],"derivedFrom":[subQ1,subQ0]})])]});}
            var Q53;
            {var subQ0=sQuery(id+"F0.wireOp",EDGE,"E12.right");var subQ1=sQuery(id+"F0.wireOp",EDGE,"E0");Q53=makeQuery(id+"F1.opExtrude","SWEPT_EDGE",EDGE,{"disambiguationData":[OSD([subQ1,subQ0]),TDD([makeQuery(id+"F0.imprint","INTERSECT",VERTEX,{"disambiguationData":[OD(0.0)],"derivedFrom":[subQ1,subQ0]})])]});}
            var Q54;
            {var subQ0=sQuery(id+"F0.wireOp",EDGE,"E14.right");var subQ1=sQuery(id+"F0.wireOp",EDGE,"E0");Q54=makeQuery(id+"F1.opExtrude","SWEPT_EDGE",EDGE,{"disambiguationData":[OSD([subQ1,subQ0]),TDD([makeQuery(id+"F0.imprint","INTERSECT",VERTEX,{"disambiguationData":[OD(0.0)],"derivedFrom":[subQ1,subQ0]})])]});}
            var Q55;
            {var subQ0=sQuery(id+"F0.wireOp",EDGE,"E18.right");var subQ1=sQuery(id+"F0.wireOp",EDGE,"E0");Q55=makeQuery(id+"F1.opExtrude","SWEPT_EDGE",EDGE,{"disambiguationData":[OSD([subQ1,subQ0]),TDD([makeQuery(id+"F0.imprint","INTERSECT",VERTEX,{"disambiguationData":[OD(1.0)],"derivedFrom":[subQ1,subQ0]})])]});}
            var Q56;
            {var subQ0=sQuery(id+"F0.wireOp",EDGE,"E16.left");var subQ1=sQuery(id+"F0.wireOp",EDGE,"E0");Q56=makeQuery(id+"F1.opExtrude","SWEPT_EDGE",EDGE,{"disambiguationData":[OSD([subQ1,subQ0]),TDD([makeQuery(id+"F0.imprint","INTERSECT",VERTEX,{"disambiguationData":[OD(1.0)],"derivedFrom":[subQ1,subQ0]})])]});}
            var Q57;
            {var subQ0=sQuery(id+"F0.wireOp",EDGE,"E15.right");var subQ1=sQuery(id+"F0.wireOp",EDGE,"E0");Q57=makeQuery(id+"F1.opExtrude","SWEPT_EDGE",EDGE,{"disambiguationData":[OSD([subQ1,subQ0]),TDD([makeQuery(id+"F0.imprint","INTERSECT",VERTEX,{"disambiguationData":[OD(0.0)],"derivedFrom":[subQ1,subQ0]})])]});}
            var Q58;
            {var subQ0=sQuery(id+"F0.wireOp",EDGE,"E20.left");var subQ1=sQuery(id+"F0.wireOp",EDGE,"E0");Q58=makeQuery(id+"F1.opExtrude","SWEPT_EDGE",EDGE,{"disambiguationData":[OSD([subQ1,subQ0]),TDD([makeQuery(id+"F0.imprint","INTERSECT",VERTEX,{"disambiguationData":[OD(1.0)],"derivedFrom":[subQ1,subQ0]})])]});}
            var Q59;
            {var subQ0=sQuery(id+"F0.wireOp",EDGE,"E17.left");var subQ1=sQuery(id+"F0.wireOp",EDGE,"E0");Q59=makeQuery(id+"F1.opExtrude","SWEPT_EDGE",EDGE,{"disambiguationData":[OSD([subQ1,subQ0]),TDD([makeQuery(id+"F0.imprint","INTERSECT",VERTEX,{"disambiguationData":[OD(0.0)],"derivedFrom":[subQ1,subQ0]})])]});}
            fillet(context, id + "F3", {"entities" : qUnion([Q0, Q1, Q2, Q3, Q4, Q5, Q6, Q7, Q8, Q9, Q10, Q11, Q12, Q13, Q14, Q15, Q16, Q17, Q18, Q19, Q20, Q21, Q22, Q23, Q24, Q25, Q26, Q27, Q28, Q29, Q30, Q31, Q32, Q33, Q34, Q35, Q36, Q37, Q38, Q39, Q40, Q41, Q42, Q43, Q44, Q45, Q46, Q47, Q48, Q49, Q50, Q51, Q52, Q53, Q54, Q55, Q56, Q57, Q58, Q59]), "radius" : 3 * mm, "tangentPropagation" : true, "allowEdgeOverflow" : false});
        }
        {
            var Q0;
            Q0=qCreatedBy(makeId("Top.planeOp"),FACE);
            var sketch = newSketch(context, id + "F4", { "sketchPlane" : qUnion([Q0])});
            skCircle(sketch, "E23", {"center": v(0, 0) * mm, "radius": 56 * mm});
            skCircle(sketch, "E24", {"center": v(0, 0) * mm, "radius": 55 * mm});
            skLineSegment(sketch, "E25", {"start": v(0, 75.16) * mm, "end": v(0, -75.72) * mm, "construction": true});
            skLineSegment(sketch, "E26", {"start": v(-78.17, 0) * mm, "end": v(81.81, 0) * mm, "construction": true});
            skLineSegment(sketch, "E27", {"start": v(0, 0) * mm, "end": v(-70.05, 40.44) * mm, "construction": true});
            skLineSegment(sketch, "E28", {"start": v(0, 0) * mm, "end": v(72.4, -41.8) * mm, "construction": true});
            skLineSegment(sketch, "E29", {"start": v(0, 0) * mm, "end": v(70.53, 40.72) * mm, "construction": true});
            skLineSegment(sketch, "E30", {"start": v(0, 0) * mm, "end": v(-71.48, -41.27) * mm, "construction": true});
            skCircle(sketch, "E31", {"center": v(0, 56) * mm, "radius": 2.25 * mm});
            skCircle(sketch, "E32", {"center": v(0, 56) * mm, "radius": 1 * mm});
            skCircle(sketch, "E33", {"center": v(0, -56) * mm, "radius": 2.25 * mm});
            skLineSegment(sketch, "E34.bottom", {"start": v(0, -57.27) * mm, "end": v(-1.27, -56) * mm});
            skLineSegment(sketch, "E34.top", {"start": v(1.27, -56) * mm, "end": v(0, -54.73) * mm});
            skLineSegment(sketch, "E34.left", {"start": v(0, -57.27) * mm, "end": v(1.27, -56) * mm});
            skLineSegment(sketch, "E34.right", {"start": v(-1.27, -56) * mm, "end": v(0, -54.73) * mm});
            skCircle(sketch, "E35", {"center": v(-48.5, -28) * mm, "radius": 2.25 * mm});
            skCircle(sketch, "E36", {"center": v(-48.5, -28) * mm, "radius": 1 * mm});
            skCircle(sketch, "E37", {"center": v(-48.5, 28) * mm, "radius": 2.25 * mm});
            skCircle(sketch, "E38", {"center": v(-48.5, 28) * mm, "radius": 1 * mm});
            skCircle(sketch, "E39", {"center": v(48.5, 28) * mm, "radius": 2.25 * mm});
            skCircle(sketch, "E40", {"center": v(48.5, 28) * mm, "radius": 1 * mm});
            skCircle(sketch, "E41", {"center": v(48.5, -28) * mm, "radius": 2.25 * mm});
            skCircle(sketch, "E42", {"center": v(48.5, -28) * mm, "radius": 1 * mm});
            skSolve(sketch);
        }
        {
            var Q0;
            {var subQ0=sQuery(id+"F4.wireOp",EDGE,"E41");var subQ1=sQuery(id+"F4.wireOp",EDGE,"E23");var subQ2=makeQuery(id+"F4.imprint","INTERSECT",VERTEX,{"disambiguationData":[OD(0.0)],"derivedFrom":[subQ1,subQ0]});Q0=makeQuery(id+"F4.imprint","IMPRINT",FACE,{"disambiguationData":[TD([[makeQuery(id+"F4.imprint","IMPRINT",EDGE,{"disambiguationData":[TD([[subQ2,-1.0]])],"derivedFrom":subQ1}),-1.0]])]});}
            var Q1;
            {var subQ0=sQuery(id+"F4.wireOp",EDGE,"E41");var subQ1=sQuery(id+"F4.wireOp",EDGE,"E23");var subQ2=makeQuery(id+"F4.imprint","INTERSECT",VERTEX,{"disambiguationData":[OD(1.0)],"derivedFrom":[subQ1,subQ0]});Q1=makeQuery(id+"F4.imprint","IMPRINT",FACE,{"disambiguationData":[TD([[makeQuery(id+"F4.imprint","IMPRINT",EDGE,{"disambiguationData":[TD([[subQ2,1.0]])],"derivedFrom":subQ1}),1.0]])]});}
            var Q2;
            {var subQ0=sQuery(id+"F4.wireOp",EDGE,"E41");var subQ1=sQuery(id+"F4.wireOp",EDGE,"E23");var subQ2=makeQuery(id+"F4.imprint","INTERSECT",VERTEX,{"disambiguationData":[OD(0.0)],"derivedFrom":[subQ1,subQ0]});Q2=makeQuery(id+"F4.imprint","IMPRINT",FACE,{"disambiguationData":[TD([[makeQuery(id+"F4.imprint","IMPRINT",EDGE,{"disambiguationData":[TD([[subQ2,-1.0]])],"derivedFrom":subQ1}),1.0]])]});}
            var Q3;
            {var subQ0=sQuery(id+"F4.wireOp",EDGE,"E41");var subQ1=sQuery(id+"F4.wireOp",EDGE,"E24");var subQ2=makeQuery(id+"F4.imprint","INTERSECT",VERTEX,{"disambiguationData":[OD(0.0)],"derivedFrom":[subQ1,subQ0]});Q3=makeQuery(id+"F4.imprint","IMPRINT",FACE,{"disambiguationData":[TD([[makeQuery(id+"F4.imprint","IMPRINT",EDGE,{"disambiguationData":[TD([[subQ2,-1.0]])],"derivedFrom":subQ1}),1.0]])]});}
            var Q4;
            {var subQ0=sQuery(id+"F4.wireOp",EDGE,"E39");var subQ1=sQuery(id+"F4.wireOp",EDGE,"E23");var subQ2=makeQuery(id+"F4.imprint","INTERSECT",VERTEX,{"disambiguationData":[OD(0.0)],"derivedFrom":[subQ1,subQ0]});Q4=makeQuery(id+"F4.imprint","IMPRINT",FACE,{"disambiguationData":[TD([[makeQuery(id+"F4.imprint","IMPRINT",EDGE,{"disambiguationData":[TD([[subQ2,-1.0]])],"derivedFrom":subQ1}),-1.0]])]});}
            var Q5;
            {var subQ0=sQuery(id+"F4.wireOp",EDGE,"E24");var subQ1=makeQuery(id+"F4.imprint","INTERSECT",VERTEX,{"derivedFrom":[subQ0,sQuery(id+"F4.wireOp",EDGE,"E40")]});Q5=makeQuery(id+"F4.imprint","IMPRINT",FACE,{"disambiguationData":[TD([[makeQuery(id+"F4.imprint","IMPRINT",EDGE,{"disambiguationData":[TD([[subQ1,1.0]])],"derivedFrom":subQ0}),1.0]])]});}
            var Q6;
            {var subQ0=sQuery(id+"F4.wireOp",EDGE,"E39");var subQ1=sQuery(id+"F4.wireOp",EDGE,"E23");var subQ2=makeQuery(id+"F4.imprint","INTERSECT",VERTEX,{"disambiguationData":[OD(1.0)],"derivedFrom":[subQ1,subQ0]});Q6=makeQuery(id+"F4.imprint","IMPRINT",FACE,{"disambiguationData":[TD([[makeQuery(id+"F4.imprint","IMPRINT",EDGE,{"disambiguationData":[TD([[subQ2,1.0]])],"derivedFrom":subQ1}),1.0]])]});}
            var Q7;
            {var subQ0=sQuery(id+"F4.wireOp",EDGE,"E39");var subQ1=sQuery(id+"F4.wireOp",EDGE,"E23");var subQ2=makeQuery(id+"F4.imprint","INTERSECT",VERTEX,{"disambiguationData":[OD(0.0)],"derivedFrom":[subQ1,subQ0]});Q7=makeQuery(id+"F4.imprint","IMPRINT",FACE,{"disambiguationData":[TD([[makeQuery(id+"F4.imprint","IMPRINT",EDGE,{"disambiguationData":[TD([[subQ2,-1.0]])],"derivedFrom":subQ1}),1.0]])]});}
            var Q8;
            {var subQ0=sQuery(id+"F4.wireOp",EDGE,"E34.bottom");Q8=makeQuery(id+"F4.imprint","IMPRINT",FACE,{"disambiguationData":[TD([[makeQuery(id+"F4.imprint","IMPRINT",EDGE,{"derivedFrom":subQ0}),1.0]])]});}
            var Q9;
            {var subQ0=sQuery(id+"F4.wireOp",EDGE,"E33");var subQ1=sQuery(id+"F4.wireOp",EDGE,"E23");var subQ2=makeQuery(id+"F4.imprint","INTERSECT",VERTEX,{"disambiguationData":[OD(1.0)],"derivedFrom":[subQ1,subQ0]});Q9=makeQuery(id+"F4.imprint","IMPRINT",FACE,{"disambiguationData":[TD([[makeQuery(id+"F4.imprint","IMPRINT",EDGE,{"disambiguationData":[TD([[subQ2,1.0]])],"derivedFrom":subQ1}),1.0]])]});}
            var Q10;
            {var subQ0=sQuery(id+"F4.wireOp",EDGE,"E33");var subQ1=sQuery(id+"F4.wireOp",EDGE,"E23");var subQ2=makeQuery(id+"F4.imprint","INTERSECT",VERTEX,{"disambiguationData":[OD(0.0)],"derivedFrom":[subQ1,subQ0]});Q10=makeQuery(id+"F4.imprint","IMPRINT",FACE,{"disambiguationData":[TD([[makeQuery(id+"F4.imprint","IMPRINT",EDGE,{"disambiguationData":[TD([[subQ2,-1.0]])],"derivedFrom":subQ1}),1.0]])]});}
            var Q11;
            {var subQ3=sQuery(id+"F4.wireOp",EDGE,"E24");var subQ5=sQuery(id+"F4.wireOp",EDGE,"E33");var subQ7=makeQuery(id+"F4.imprint","INTERSECT",VERTEX,{"disambiguationData":[OD(0.0)],"derivedFrom":[subQ3,subQ5]});Q11=makeQuery(id+"F4.imprint","IMPRINT",FACE,{"disambiguationData":[TD([[makeQuery(id+"F4.imprint","IMPRINT",EDGE,{"disambiguationData":[TD([[subQ7,-1.0]])],"derivedFrom":subQ3}),1.0]])]});}
            var Q12;
            {var subQ0=sQuery(id+"F4.wireOp",EDGE,"E35");var subQ1=sQuery(id+"F4.wireOp",EDGE,"E23");var subQ2=makeQuery(id+"F4.imprint","INTERSECT",VERTEX,{"disambiguationData":[OD(0.0)],"derivedFrom":[subQ1,subQ0]});Q12=makeQuery(id+"F4.imprint","IMPRINT",FACE,{"disambiguationData":[TD([[makeQuery(id+"F4.imprint","IMPRINT",EDGE,{"disambiguationData":[TD([[subQ2,-1.0]])],"derivedFrom":subQ1}),-1.0]])]});}
            var Q13;
            {var subQ0=sQuery(id+"F4.wireOp",EDGE,"E35");var subQ1=sQuery(id+"F4.wireOp",EDGE,"E23");var subQ2=makeQuery(id+"F4.imprint","INTERSECT",VERTEX,{"disambiguationData":[OD(0.0)],"derivedFrom":[subQ1,subQ0]});Q13=makeQuery(id+"F4.imprint","IMPRINT",FACE,{"disambiguationData":[TD([[makeQuery(id+"F4.imprint","IMPRINT",EDGE,{"disambiguationData":[TD([[subQ2,-1.0]])],"derivedFrom":subQ1}),1.0]])]});}
            var Q14;
            {var subQ0=sQuery(id+"F4.wireOp",EDGE,"E35");var subQ1=sQuery(id+"F4.wireOp",EDGE,"E23");var subQ2=makeQuery(id+"F4.imprint","INTERSECT",VERTEX,{"disambiguationData":[OD(1.0)],"derivedFrom":[subQ1,subQ0]});Q14=makeQuery(id+"F4.imprint","IMPRINT",FACE,{"disambiguationData":[TD([[makeQuery(id+"F4.imprint","IMPRINT",EDGE,{"disambiguationData":[TD([[subQ2,1.0]])],"derivedFrom":subQ1}),1.0]])]});}
            var Q15;
            {var subQ0=sQuery(id+"F4.wireOp",EDGE,"E35");var subQ1=sQuery(id+"F4.wireOp",EDGE,"E24");var subQ2=makeQuery(id+"F4.imprint","INTERSECT",VERTEX,{"disambiguationData":[OD(0.0)],"derivedFrom":[subQ1,subQ0]});Q15=makeQuery(id+"F4.imprint","IMPRINT",FACE,{"disambiguationData":[TD([[makeQuery(id+"F4.imprint","IMPRINT",EDGE,{"disambiguationData":[TD([[subQ2,-1.0]])],"derivedFrom":subQ1}),1.0]])]});}
            var Q16;
            {var subQ0=sQuery(id+"F4.wireOp",EDGE,"E37");var subQ1=sQuery(id+"F4.wireOp",EDGE,"E23");var subQ2=makeQuery(id+"F4.imprint","INTERSECT",VERTEX,{"disambiguationData":[OD(0.0)],"derivedFrom":[subQ1,subQ0]});Q16=makeQuery(id+"F4.imprint","IMPRINT",FACE,{"disambiguationData":[TD([[makeQuery(id+"F4.imprint","IMPRINT",EDGE,{"disambiguationData":[TD([[subQ2,-1.0]])],"derivedFrom":subQ1}),-1.0]])]});}
            var Q17;
            {var subQ0=sQuery(id+"F4.wireOp",EDGE,"E37");var subQ1=sQuery(id+"F4.wireOp",EDGE,"E23");var subQ2=makeQuery(id+"F4.imprint","INTERSECT",VERTEX,{"disambiguationData":[OD(0.0)],"derivedFrom":[subQ1,subQ0]});Q17=makeQuery(id+"F4.imprint","IMPRINT",FACE,{"disambiguationData":[TD([[makeQuery(id+"F4.imprint","IMPRINT",EDGE,{"disambiguationData":[TD([[subQ2,-1.0]])],"derivedFrom":subQ1}),1.0]])]});}
            var Q18;
            {var subQ0=sQuery(id+"F4.wireOp",EDGE,"E37");var subQ1=sQuery(id+"F4.wireOp",EDGE,"E23");var subQ2=makeQuery(id+"F4.imprint","INTERSECT",VERTEX,{"disambiguationData":[OD(1.0)],"derivedFrom":[subQ1,subQ0]});Q18=makeQuery(id+"F4.imprint","IMPRINT",FACE,{"disambiguationData":[TD([[makeQuery(id+"F4.imprint","IMPRINT",EDGE,{"disambiguationData":[TD([[subQ2,1.0]])],"derivedFrom":subQ1}),1.0]])]});}
            var Q19;
            {var subQ0=sQuery(id+"F4.wireOp",EDGE,"E37");var subQ1=sQuery(id+"F4.wireOp",EDGE,"E24");var subQ2=makeQuery(id+"F4.imprint","INTERSECT",VERTEX,{"disambiguationData":[OD(0.0)],"derivedFrom":[subQ1,subQ0]});Q19=makeQuery(id+"F4.imprint","IMPRINT",FACE,{"disambiguationData":[TD([[makeQuery(id+"F4.imprint","IMPRINT",EDGE,{"disambiguationData":[TD([[subQ2,-1.0]])],"derivedFrom":subQ1}),1.0]])]});}
            var Q20;
            {var subQ0=sQuery(id+"F4.wireOp",EDGE,"E31");var subQ1=sQuery(id+"F4.wireOp",EDGE,"E24");var subQ2=makeQuery(id+"F4.imprint","INTERSECT",VERTEX,{"disambiguationData":[OD(0.0)],"derivedFrom":[subQ1,subQ0]});Q20=makeQuery(id+"F4.imprint","IMPRINT",FACE,{"disambiguationData":[TD([[makeQuery(id+"F4.imprint","IMPRINT",EDGE,{"disambiguationData":[TD([[subQ2,-1.0]])],"derivedFrom":subQ1}),1.0]])]});}
            var Q21;
            {var subQ0=sQuery(id+"F4.wireOp",EDGE,"E31");var subQ1=sQuery(id+"F4.wireOp",EDGE,"E23");var subQ2=makeQuery(id+"F4.imprint","INTERSECT",VERTEX,{"disambiguationData":[OD(1.0)],"derivedFrom":[subQ1,subQ0]});Q21=makeQuery(id+"F4.imprint","IMPRINT",FACE,{"disambiguationData":[TD([[makeQuery(id+"F4.imprint","IMPRINT",EDGE,{"disambiguationData":[TD([[subQ2,1.0]])],"derivedFrom":subQ1}),1.0]])]});}
            var Q22;
            {var subQ0=sQuery(id+"F4.wireOp",EDGE,"E31");var subQ1=sQuery(id+"F4.wireOp",EDGE,"E23");var subQ2=makeQuery(id+"F4.imprint","INTERSECT",VERTEX,{"disambiguationData":[OD(0.0)],"derivedFrom":[subQ1,subQ0]});Q22=makeQuery(id+"F4.imprint","IMPRINT",FACE,{"disambiguationData":[TD([[makeQuery(id+"F4.imprint","IMPRINT",EDGE,{"disambiguationData":[TD([[subQ2,-1.0]])],"derivedFrom":subQ1}),1.0]])]});}
            var Q23;
            {var subQ0=sQuery(id+"F4.wireOp",EDGE,"E31");var subQ1=sQuery(id+"F4.wireOp",EDGE,"E23");var subQ2=makeQuery(id+"F4.imprint","INTERSECT",VERTEX,{"disambiguationData":[OD(0.0)],"derivedFrom":[subQ1,subQ0]});Q23=makeQuery(id+"F4.imprint","IMPRINT",FACE,{"disambiguationData":[TD([[makeQuery(id+"F4.imprint","IMPRINT",EDGE,{"disambiguationData":[TD([[subQ2,-1.0]])],"derivedFrom":subQ1}),-1.0]])]});}
            extrude(context, id + "F5", {"entities" : qUnion([Q0, Q1, Q2, Q3, Q4, Q5, Q6, Q7, Q8, Q9, Q10, Q11, Q12, Q13, Q14, Q15, Q16, Q17, Q18, Q19, Q20, Q21, Q22, Q23]), "operationType" : NewBodyOperationType.ADD, "depth" : 10 * mm, "offsetDistance" : 25 * mm});
        }
        {
            var Q0;
            {var subQ0=sQuery(id+"F4.wireOp",EDGE,"E32");var subQ1=sQuery(id+"F4.wireOp",EDGE,"E23");var subQ2=makeQuery(id+"F4.imprint","INTERSECT",VERTEX,{"disambiguationData":[OD(0.0)],"derivedFrom":[subQ1,subQ0]});Q0=makeQuery(id+"F4.imprint","IMPRINT",FACE,{"disambiguationData":[TD([[makeQuery(id+"F4.imprint","IMPRINT",EDGE,{"disambiguationData":[TD([[subQ2,-1.0]])],"derivedFrom":subQ1}),-1.0]])]});}
            var Q1;
            {var subQ0=sQuery(id+"F4.wireOp",EDGE,"E32");var subQ1=sQuery(id+"F4.wireOp",EDGE,"E23");var subQ2=makeQuery(id+"F4.imprint","INTERSECT",VERTEX,{"disambiguationData":[OD(0.0)],"derivedFrom":[subQ1,subQ0]});Q1=makeQuery(id+"F4.imprint","IMPRINT",FACE,{"disambiguationData":[TD([[makeQuery(id+"F4.imprint","IMPRINT",EDGE,{"disambiguationData":[TD([[subQ2,-1.0]])],"derivedFrom":subQ1}),1.0]])]});}
            var Q2;
            {var subQ0=sQuery(id+"F4.wireOp",EDGE,"E40");var subQ1=sQuery(id+"F4.wireOp",EDGE,"E23");var subQ2=makeQuery(id+"F4.imprint","INTERSECT",VERTEX,{"disambiguationData":[OD(0.0)],"derivedFrom":[subQ1,subQ0]});Q2=makeQuery(id+"F4.imprint","IMPRINT",FACE,{"disambiguationData":[TD([[makeQuery(id+"F4.imprint","IMPRINT",EDGE,{"disambiguationData":[TD([[subQ2,-1.0]])],"derivedFrom":subQ1}),1.0]])]});}
            var Q3;
            {var subQ0=sQuery(id+"F4.wireOp",EDGE,"E40");var subQ1=sQuery(id+"F4.wireOp",EDGE,"E23");var subQ2=makeQuery(id+"F4.imprint","INTERSECT",VERTEX,{"disambiguationData":[OD(0.0)],"derivedFrom":[subQ1,subQ0]});Q3=makeQuery(id+"F4.imprint","IMPRINT",FACE,{"disambiguationData":[TD([[makeQuery(id+"F4.imprint","IMPRINT",EDGE,{"disambiguationData":[TD([[subQ2,-1.0]])],"derivedFrom":subQ1}),-1.0]])]});}
            var Q4;
            {var subQ0=sQuery(id+"F4.wireOp",EDGE,"E42");var subQ1=sQuery(id+"F4.wireOp",EDGE,"E23");var subQ2=makeQuery(id+"F4.imprint","INTERSECT",VERTEX,{"disambiguationData":[OD(0.0)],"derivedFrom":[subQ1,subQ0]});Q4=makeQuery(id+"F4.imprint","IMPRINT",FACE,{"disambiguationData":[TD([[makeQuery(id+"F4.imprint","IMPRINT",EDGE,{"disambiguationData":[TD([[subQ2,-1.0]])],"derivedFrom":subQ1}),-1.0]])]});}
            var Q5;
            {var subQ0=sQuery(id+"F4.wireOp",EDGE,"E42");var subQ1=sQuery(id+"F4.wireOp",EDGE,"E23");var subQ2=makeQuery(id+"F4.imprint","INTERSECT",VERTEX,{"disambiguationData":[OD(0.0)],"derivedFrom":[subQ1,subQ0]});Q5=makeQuery(id+"F4.imprint","IMPRINT",FACE,{"disambiguationData":[TD([[makeQuery(id+"F4.imprint","IMPRINT",EDGE,{"disambiguationData":[TD([[subQ2,-1.0]])],"derivedFrom":subQ1}),1.0]])]});}
            var Q6;
            {var subQ4=sQuery(id+"F4.wireOp",EDGE,"E34.bottom");Q6=makeQuery(id+"F4.imprint","IMPRINT",FACE,{"disambiguationData":[TD([[makeQuery(id+"F4.imprint","IMPRINT",EDGE,{"derivedFrom":subQ4}),-1.0]])]});}
            var Q7;
            {var subQ0=sQuery(id+"F4.wireOp",EDGE,"E34.right");var subQ1=sQuery(id+"F4.wireOp",EDGE,"E23");var subQ2=makeQuery(id+"F4.imprint","INTERSECT",VERTEX,{"derivedFrom":[subQ1,subQ0]});Q7=makeQuery(id+"F4.imprint","IMPRINT",FACE,{"disambiguationData":[TD([[makeQuery(id+"F4.imprint","IMPRINT",EDGE,{"disambiguationData":[TD([[subQ2,-1.0]])],"derivedFrom":subQ1}),1.0]])]});}
            var Q8;
            {var subQ0=sQuery(id+"F4.wireOp",EDGE,"E34.right");var subQ1=sQuery(id+"F4.wireOp",EDGE,"E24");var subQ2=makeQuery(id+"F4.imprint","INTERSECT",VERTEX,{"derivedFrom":[subQ1,subQ0]});Q8=makeQuery(id+"F4.imprint","IMPRINT",FACE,{"disambiguationData":[TD([[makeQuery(id+"F4.imprint","IMPRINT",EDGE,{"disambiguationData":[TD([[subQ2,-1.0]])],"derivedFrom":subQ1}),1.0]])]});}
            var Q9;
            {var subQ0=sQuery(id+"F4.wireOp",EDGE,"E36");var subQ1=sQuery(id+"F4.wireOp",EDGE,"E23");var subQ2=makeQuery(id+"F4.imprint","INTERSECT",VERTEX,{"disambiguationData":[OD(0.0)],"derivedFrom":[subQ1,subQ0]});Q9=makeQuery(id+"F4.imprint","IMPRINT",FACE,{"disambiguationData":[TD([[makeQuery(id+"F4.imprint","IMPRINT",EDGE,{"disambiguationData":[TD([[subQ2,-1.0]])],"derivedFrom":subQ1}),1.0]])]});}
            var Q10;
            {var subQ0=sQuery(id+"F4.wireOp",EDGE,"E36");var subQ1=sQuery(id+"F4.wireOp",EDGE,"E23");var subQ2=makeQuery(id+"F4.imprint","INTERSECT",VERTEX,{"disambiguationData":[OD(0.0)],"derivedFrom":[subQ1,subQ0]});Q10=makeQuery(id+"F4.imprint","IMPRINT",FACE,{"disambiguationData":[TD([[makeQuery(id+"F4.imprint","IMPRINT",EDGE,{"disambiguationData":[TD([[subQ2,-1.0]])],"derivedFrom":subQ1}),-1.0]])]});}
            var Q11;
            {var subQ0=sQuery(id+"F4.wireOp",EDGE,"E38");var subQ1=sQuery(id+"F4.wireOp",EDGE,"E23");var subQ2=makeQuery(id+"F4.imprint","INTERSECT",VERTEX,{"disambiguationData":[OD(0.0)],"derivedFrom":[subQ1,subQ0]});Q11=makeQuery(id+"F4.imprint","IMPRINT",FACE,{"disambiguationData":[TD([[makeQuery(id+"F4.imprint","IMPRINT",EDGE,{"disambiguationData":[TD([[subQ2,-1.0]])],"derivedFrom":subQ1}),-1.0]])]});}
            var Q12;
            {var subQ0=sQuery(id+"F4.wireOp",EDGE,"E38");var subQ1=sQuery(id+"F4.wireOp",EDGE,"E23");var subQ2=makeQuery(id+"F4.imprint","INTERSECT",VERTEX,{"disambiguationData":[OD(0.0)],"derivedFrom":[subQ1,subQ0]});Q12=makeQuery(id+"F4.imprint","IMPRINT",FACE,{"disambiguationData":[TD([[makeQuery(id+"F4.imprint","IMPRINT",EDGE,{"disambiguationData":[TD([[subQ2,-1.0]])],"derivedFrom":subQ1}),1.0]])]});}
            extrude(context, id + "F6", {"entities" : qUnion([Q0, Q1, Q2, Q3, Q4, Q5, Q6, Q7, Q8, Q9, Q10, Q11, Q12]), "operationType" : NewBodyOperationType.ADD, "depth" : 12.5 * mm, "offsetDistance" : 25 * mm});
        }
        {
            var Q0;
            {var subQ0=sQuery(id+"F0.wireOp",EDGE,"E1");Q0=makeQuery(id+"F5.boolean.opBoolean","INTERSECT",EDGE,{"derivedFrom":[makeQuery(id+"F1.opExtrude","SWEPT_FACE",FACE,{"disambiguationData":[OSD([subQ0]),TDD([makeQuery(id+"F0.imprint","IMPRINT",EDGE,{"disambiguationData":[TD([[makeQuery(id+"F0.imprint","INTERSECT",VERTEX,{"derivedFrom":[subQ0,sQuery(id+"F0.wireOp",EDGE,"E8.bottom"),sQuery(id+"F0.wireOp",EDGE,"E8.left")]}),-1.0]])],"derivedFrom":subQ0})])]}),makeQuery(id+"F5.opExtrude","SWEPT_FACE",FACE,{"disambiguationData":[OSD([sQuery(id+"F4.wireOp",EDGE,"E33")])]})]});}
            var Q1;
            {var subQ0=sQuery(id+"F0.wireOp",EDGE,"E1");Q1=makeQuery(id+"F5.boolean.opBoolean","INTERSECT",EDGE,{"derivedFrom":[makeQuery(id+"F1.opExtrude","SWEPT_FACE",FACE,{"disambiguationData":[OSD([subQ0]),TDD([makeQuery(id+"F0.imprint","IMPRINT",EDGE,{"disambiguationData":[TD([[makeQuery(id+"F0.imprint","INTERSECT",VERTEX,{"derivedFrom":[subQ0,sQuery(id+"F0.wireOp",EDGE,"E8.bottom"),sQuery(id+"F0.wireOp",EDGE,"E8.right")]}),1.0]])],"derivedFrom":subQ0})])]}),makeQuery(id+"F5.opExtrude","SWEPT_FACE",FACE,{"disambiguationData":[OSD([sQuery(id+"F4.wireOp",EDGE,"E33")])]})]});}
            var Q2;
            {var subQ0=sQuery(id+"F0.wireOp",EDGE,"E1");Q2=makeQuery(id+"F5.boolean.opBoolean","INTERSECT",EDGE,{"derivedFrom":[makeQuery(id+"F1.opExtrude","SWEPT_FACE",FACE,{"disambiguationData":[OSD([subQ0]),TDD([makeQuery(id+"F0.imprint","IMPRINT",EDGE,{"disambiguationData":[TD([[makeQuery(id+"F0.imprint","INTERSECT",VERTEX,{"derivedFrom":[subQ0,sQuery(id+"F0.wireOp",EDGE,"E17.bottom"),sQuery(id+"F0.wireOp",EDGE,"E17.right")]}),1.0]])],"derivedFrom":subQ0})])]}),makeQuery(id+"F5.opExtrude","SWEPT_FACE",FACE,{"disambiguationData":[OSD([sQuery(id+"F4.wireOp",EDGE,"E41")])]})]});}
            var Q3;
            {var subQ0=sQuery(id+"F0.wireOp",EDGE,"E1");Q3=makeQuery(id+"F5.boolean.opBoolean","INTERSECT",EDGE,{"derivedFrom":[makeQuery(id+"F1.opExtrude","SWEPT_FACE",FACE,{"disambiguationData":[OSD([subQ0]),TDD([makeQuery(id+"F0.imprint","IMPRINT",EDGE,{"disambiguationData":[TD([[makeQuery(id+"F0.imprint","INTERSECT",VERTEX,{"derivedFrom":[subQ0,sQuery(id+"F0.wireOp",EDGE,"E13.bottom"),sQuery(id+"F0.wireOp",EDGE,"E13.right")]}),1.0]])],"derivedFrom":subQ0})])]}),makeQuery(id+"F5.opExtrude","SWEPT_FACE",FACE,{"disambiguationData":[OSD([sQuery(id+"F4.wireOp",EDGE,"E39")])]})]});}
            var Q4;
            {var subQ0=sQuery(id+"F0.wireOp",EDGE,"E1");Q4=makeQuery(id+"F5.boolean.opBoolean","INTERSECT",EDGE,{"derivedFrom":[makeQuery(id+"F1.opExtrude","SWEPT_FACE",FACE,{"disambiguationData":[OSD([subQ0]),TDD([makeQuery(id+"F0.imprint","IMPRINT",EDGE,{"disambiguationData":[TD([[makeQuery(id+"F0.imprint","INTERSECT",VERTEX,{"derivedFrom":[subQ0,sQuery(id+"F0.wireOp",EDGE,"E12.top"),sQuery(id+"F0.wireOp",EDGE,"E12.left")]}),1.0]])],"derivedFrom":subQ0})])]}),makeQuery(id+"F5.opExtrude","SWEPT_FACE",FACE,{"disambiguationData":[OSD([sQuery(id+"F4.wireOp",EDGE,"E39")])]})]});}
            var Q5;
            {var subQ0=sQuery(id+"F0.wireOp",EDGE,"E1");Q5=makeQuery(id+"F5.boolean.opBoolean","INTERSECT",EDGE,{"derivedFrom":[makeQuery(id+"F1.opExtrude","SWEPT_FACE",FACE,{"disambiguationData":[OSD([subQ0]),TDD([makeQuery(id+"F0.imprint","IMPRINT",EDGE,{"disambiguationData":[TD([[makeQuery(id+"F0.imprint","INTERSECT",VERTEX,{"derivedFrom":[subQ0,sQuery(id+"F0.wireOp",EDGE,"E18.bottom"),sQuery(id+"F0.wireOp",EDGE,"E18.right")]}),1.0]])],"derivedFrom":subQ0})])]}),makeQuery(id+"F5.opExtrude","SWEPT_FACE",FACE,{"disambiguationData":[OSD([sQuery(id+"F4.wireOp",EDGE,"E41")])]})]});}
            var Q6;
            {var subQ0=sQuery(id+"F0.wireOp",EDGE,"E1");Q6=makeQuery(id+"F5.boolean.opBoolean","INTERSECT",EDGE,{"derivedFrom":[makeQuery(id+"F1.opExtrude","SWEPT_FACE",FACE,{"disambiguationData":[OSD([subQ0]),TDD([makeQuery(id+"F0.imprint","IMPRINT",EDGE,{"disambiguationData":[TD([[makeQuery(id+"F0.imprint","INTERSECT",VERTEX,{"derivedFrom":[subQ0,sQuery(id+"F0.wireOp",EDGE,"E8.top"),sQuery(id+"F0.wireOp",EDGE,"E8.left")]}),1.0]])],"derivedFrom":subQ0})])]}),makeQuery(id+"F5.opExtrude","SWEPT_FACE",FACE,{"disambiguationData":[OSD([sQuery(id+"F4.wireOp",EDGE,"E31")])]})]});}
            var Q7;
            {var subQ0=sQuery(id+"F0.wireOp",EDGE,"E1");Q7=makeQuery(id+"F5.boolean.opBoolean","INTERSECT",EDGE,{"derivedFrom":[makeQuery(id+"F1.opExtrude","SWEPT_FACE",FACE,{"disambiguationData":[OSD([subQ0]),TDD([makeQuery(id+"F0.imprint","IMPRINT",EDGE,{"disambiguationData":[TD([[makeQuery(id+"F0.imprint","INTERSECT",VERTEX,{"derivedFrom":[subQ0,sQuery(id+"F0.wireOp",EDGE,"E8.top"),sQuery(id+"F0.wireOp",EDGE,"E8.right")]}),-1.0]])],"derivedFrom":subQ0})])]}),makeQuery(id+"F5.opExtrude","SWEPT_FACE",FACE,{"disambiguationData":[OSD([sQuery(id+"F4.wireOp",EDGE,"E31")])]})]});}
            var Q8;
            {var subQ0=sQuery(id+"F0.wireOp",EDGE,"E1");Q8=makeQuery(id+"F5.boolean.opBoolean","INTERSECT",EDGE,{"derivedFrom":[makeQuery(id+"F1.opExtrude","SWEPT_FACE",FACE,{"disambiguationData":[OSD([subQ0]),TDD([makeQuery(id+"F0.imprint","IMPRINT",EDGE,{"disambiguationData":[TD([[makeQuery(id+"F0.imprint","INTERSECT",VERTEX,{"derivedFrom":[subQ0,sQuery(id+"F0.wireOp",EDGE,"E18.top"),sQuery(id+"F0.wireOp",EDGE,"E18.left")]}),1.0]])],"derivedFrom":subQ0})])]}),makeQuery(id+"F5.opExtrude","SWEPT_FACE",FACE,{"disambiguationData":[OSD([sQuery(id+"F4.wireOp",EDGE,"E37")])]})]});}
            var Q9;
            {var subQ0=sQuery(id+"F0.wireOp",EDGE,"E1");Q9=makeQuery(id+"F5.boolean.opBoolean","INTERSECT",EDGE,{"derivedFrom":[makeQuery(id+"F1.opExtrude","SWEPT_FACE",FACE,{"disambiguationData":[OSD([subQ0]),TDD([makeQuery(id+"F0.imprint","IMPRINT",EDGE,{"disambiguationData":[TD([[makeQuery(id+"F0.imprint","INTERSECT",VERTEX,{"derivedFrom":[subQ0,sQuery(id+"F0.wireOp",EDGE,"E17.top"),sQuery(id+"F0.wireOp",EDGE,"E17.left")]}),1.0]])],"derivedFrom":subQ0})])]}),makeQuery(id+"F5.opExtrude","SWEPT_FACE",FACE,{"disambiguationData":[OSD([sQuery(id+"F4.wireOp",EDGE,"E37")])]})]});}
            var Q10;
            {var subQ0=sQuery(id+"F0.wireOp",EDGE,"E1");Q10=makeQuery(id+"F5.boolean.opBoolean","INTERSECT",EDGE,{"derivedFrom":[makeQuery(id+"F1.opExtrude","SWEPT_FACE",FACE,{"disambiguationData":[OSD([subQ0]),TDD([makeQuery(id+"F0.imprint","IMPRINT",EDGE,{"disambiguationData":[TD([[makeQuery(id+"F0.imprint","INTERSECT",VERTEX,{"derivedFrom":[subQ0,sQuery(id+"F0.wireOp",EDGE,"E13.top"),sQuery(id+"F0.wireOp",EDGE,"E13.left")]}),1.0]])],"derivedFrom":subQ0})])]}),makeQuery(id+"F5.opExtrude","SWEPT_FACE",FACE,{"disambiguationData":[OSD([sQuery(id+"F4.wireOp",EDGE,"E35")])]})]});}
            var Q11;
            {var subQ0=sQuery(id+"F0.wireOp",EDGE,"E1");Q11=makeQuery(id+"F5.boolean.opBoolean","INTERSECT",EDGE,{"derivedFrom":[makeQuery(id+"F1.opExtrude","SWEPT_FACE",FACE,{"disambiguationData":[OSD([subQ0]),TDD([makeQuery(id+"F0.imprint","IMPRINT",EDGE,{"disambiguationData":[TD([[makeQuery(id+"F0.imprint","INTERSECT",VERTEX,{"derivedFrom":[subQ0,sQuery(id+"F0.wireOp",EDGE,"E12.bottom"),sQuery(id+"F0.wireOp",EDGE,"E12.right")]}),1.0]])],"derivedFrom":subQ0})])]}),makeQuery(id+"F5.opExtrude","SWEPT_FACE",FACE,{"disambiguationData":[OSD([sQuery(id+"F4.wireOp",EDGE,"E35")])]})]});}
            fillet(context, id + "F7", {"entities" : qUnion([Q0, Q1, Q2, Q3, Q4, Q5, Q6, Q7, Q8, Q9, Q10, Q11]), "radius" : 5 * mm, "tangentPropagation" : true, "allowEdgeOverflow" : false});
        }
        {
            var Q0;
            {var subQ0=sQuery(id+"F4.wireOp",EDGE,"E37");var subQ1=sQuery(id+"F4.wireOp",EDGE,"E23");var subQ2=makeQuery(id+"F4.imprint","INTERSECT",VERTEX,{"disambiguationData":[OD(0.0)],"derivedFrom":[subQ1,subQ0]});Q0=makeQuery(id+"F4.imprint","IMPRINT",FACE,{"disambiguationData":[TD([[makeQuery(id+"F4.imprint","IMPRINT",EDGE,{"disambiguationData":[TD([[subQ2,-1.0]])],"derivedFrom":subQ1}),-1.0]])]});}
            var Q1;
            {var subQ0=sQuery(id+"F4.wireOp",EDGE,"E31");var subQ1=sQuery(id+"F4.wireOp",EDGE,"E23");var subQ2=makeQuery(id+"F4.imprint","INTERSECT",VERTEX,{"disambiguationData":[OD(1.0)],"derivedFrom":[subQ1,subQ0]});Q1=makeQuery(id+"F4.imprint","IMPRINT",FACE,{"disambiguationData":[TD([[makeQuery(id+"F4.imprint","IMPRINT",EDGE,{"disambiguationData":[TD([[subQ2,-1.0]])],"derivedFrom":subQ1}),1.0]])]});}
            var Q2;
            {var subQ0=sQuery(id+"F4.wireOp",EDGE,"E31");var subQ1=sQuery(id+"F4.wireOp",EDGE,"E23");var subQ2=makeQuery(id+"F4.imprint","INTERSECT",VERTEX,{"disambiguationData":[OD(0.0)],"derivedFrom":[subQ1,subQ0]});Q2=makeQuery(id+"F4.imprint","IMPRINT",FACE,{"disambiguationData":[TD([[makeQuery(id+"F4.imprint","IMPRINT",EDGE,{"disambiguationData":[TD([[subQ2,-1.0]])],"derivedFrom":subQ1}),-1.0]])]});}
            var Q3;
            {var subQ0=sQuery(id+"F4.wireOp",EDGE,"E39");var subQ1=sQuery(id+"F4.wireOp",EDGE,"E23");var subQ2=makeQuery(id+"F4.imprint","INTERSECT",VERTEX,{"disambiguationData":[OD(1.0)],"derivedFrom":[subQ1,subQ0]});Q3=makeQuery(id+"F4.imprint","IMPRINT",FACE,{"disambiguationData":[TD([[makeQuery(id+"F4.imprint","IMPRINT",EDGE,{"disambiguationData":[TD([[subQ2,-1.0]])],"derivedFrom":subQ1}),1.0]])]});}
            var Q4;
            {var subQ0=sQuery(id+"F4.wireOp",EDGE,"E37");var subQ1=sQuery(id+"F4.wireOp",EDGE,"E23");var subQ2=makeQuery(id+"F4.imprint","INTERSECT",VERTEX,{"disambiguationData":[OD(0.0)],"derivedFrom":[subQ1,subQ0]});Q4=makeQuery(id+"F4.imprint","IMPRINT",FACE,{"disambiguationData":[TD([[makeQuery(id+"F4.imprint","IMPRINT",EDGE,{"disambiguationData":[TD([[subQ2,-1.0]])],"derivedFrom":subQ1}),1.0]])]});}
            var Q5;
            {var subQ0=sQuery(id+"F4.wireOp",EDGE,"E37");var subQ1=sQuery(id+"F4.wireOp",EDGE,"E23");var subQ2=makeQuery(id+"F4.imprint","INTERSECT",VERTEX,{"disambiguationData":[OD(1.0)],"derivedFrom":[subQ1,subQ0]});Q5=makeQuery(id+"F4.imprint","IMPRINT",FACE,{"disambiguationData":[TD([[makeQuery(id+"F4.imprint","IMPRINT",EDGE,{"disambiguationData":[TD([[subQ2,1.0]])],"derivedFrom":subQ1}),1.0]])]});}
            var Q6;
            {var subQ0=sQuery(id+"F4.wireOp",EDGE,"E37");var subQ1=sQuery(id+"F4.wireOp",EDGE,"E24");var subQ2=makeQuery(id+"F4.imprint","INTERSECT",VERTEX,{"disambiguationData":[OD(0.0)],"derivedFrom":[subQ1,subQ0]});Q6=makeQuery(id+"F4.imprint","IMPRINT",FACE,{"disambiguationData":[TD([[makeQuery(id+"F4.imprint","IMPRINT",EDGE,{"disambiguationData":[TD([[subQ2,-1.0]])],"derivedFrom":subQ1}),1.0]])]});}
            var Q7;
            {var subQ0=sQuery(id+"F4.wireOp",EDGE,"E31");var subQ1=sQuery(id+"F4.wireOp",EDGE,"E23");var subQ2=makeQuery(id+"F4.imprint","INTERSECT",VERTEX,{"disambiguationData":[OD(0.0)],"derivedFrom":[subQ1,subQ0]});Q7=makeQuery(id+"F4.imprint","IMPRINT",FACE,{"disambiguationData":[TD([[makeQuery(id+"F4.imprint","IMPRINT",EDGE,{"disambiguationData":[TD([[subQ2,-1.0]])],"derivedFrom":subQ1}),1.0]])]});}
            var Q8;
            {var subQ0=sQuery(id+"F4.wireOp",EDGE,"E31");var subQ1=sQuery(id+"F4.wireOp",EDGE,"E23");var subQ2=makeQuery(id+"F4.imprint","INTERSECT",VERTEX,{"disambiguationData":[OD(1.0)],"derivedFrom":[subQ1,subQ0]});Q8=makeQuery(id+"F4.imprint","IMPRINT",FACE,{"disambiguationData":[TD([[makeQuery(id+"F4.imprint","IMPRINT",EDGE,{"disambiguationData":[TD([[subQ2,1.0]])],"derivedFrom":subQ1}),1.0]])]});}
            var Q9;
            {var subQ0=sQuery(id+"F4.wireOp",EDGE,"E31");var subQ1=sQuery(id+"F4.wireOp",EDGE,"E24");var subQ2=makeQuery(id+"F4.imprint","INTERSECT",VERTEX,{"disambiguationData":[OD(0.0)],"derivedFrom":[subQ1,subQ0]});Q9=makeQuery(id+"F4.imprint","IMPRINT",FACE,{"disambiguationData":[TD([[makeQuery(id+"F4.imprint","IMPRINT",EDGE,{"disambiguationData":[TD([[subQ2,-1.0]])],"derivedFrom":subQ1}),1.0]])]});}
            var Q10;
            {var subQ0=sQuery(id+"F4.wireOp",EDGE,"E24");var subQ1=makeQuery(id+"F4.imprint","INTERSECT",VERTEX,{"derivedFrom":[subQ0,sQuery(id+"F4.wireOp",EDGE,"E40")]});Q10=makeQuery(id+"F4.imprint","IMPRINT",FACE,{"disambiguationData":[TD([[makeQuery(id+"F4.imprint","IMPRINT",EDGE,{"disambiguationData":[TD([[subQ1,1.0]])],"derivedFrom":subQ0}),1.0]])]});}
            var Q11;
            {var subQ0=sQuery(id+"F4.wireOp",EDGE,"E39");var subQ1=sQuery(id+"F4.wireOp",EDGE,"E23");var subQ2=makeQuery(id+"F4.imprint","INTERSECT",VERTEX,{"disambiguationData":[OD(1.0)],"derivedFrom":[subQ1,subQ0]});Q11=makeQuery(id+"F4.imprint","IMPRINT",FACE,{"disambiguationData":[TD([[makeQuery(id+"F4.imprint","IMPRINT",EDGE,{"disambiguationData":[TD([[subQ2,1.0]])],"derivedFrom":subQ1}),1.0]])]});}
            var Q12;
            {var subQ0=sQuery(id+"F4.wireOp",EDGE,"E39");var subQ1=sQuery(id+"F4.wireOp",EDGE,"E23");var subQ2=makeQuery(id+"F4.imprint","INTERSECT",VERTEX,{"disambiguationData":[OD(0.0)],"derivedFrom":[subQ1,subQ0]});Q12=makeQuery(id+"F4.imprint","IMPRINT",FACE,{"disambiguationData":[TD([[makeQuery(id+"F4.imprint","IMPRINT",EDGE,{"disambiguationData":[TD([[subQ2,-1.0]])],"derivedFrom":subQ1}),1.0]])]});}
            var Q13;
            {var subQ0=sQuery(id+"F4.wireOp",EDGE,"E39");var subQ1=sQuery(id+"F4.wireOp",EDGE,"E23");var subQ2=makeQuery(id+"F4.imprint","INTERSECT",VERTEX,{"disambiguationData":[OD(0.0)],"derivedFrom":[subQ1,subQ0]});Q13=makeQuery(id+"F4.imprint","IMPRINT",FACE,{"disambiguationData":[TD([[makeQuery(id+"F4.imprint","IMPRINT",EDGE,{"disambiguationData":[TD([[subQ2,-1.0]])],"derivedFrom":subQ1}),-1.0]])]});}
            var Q14;
            {var subQ0=sQuery(id+"F4.wireOp",EDGE,"E39");var subQ1=sQuery(id+"F4.wireOp",EDGE,"E23");var subQ2=makeQuery(id+"F4.imprint","INTERSECT",VERTEX,{"disambiguationData":[OD(0.0)],"derivedFrom":[subQ1,subQ0]});Q14=makeQuery(id+"F4.imprint","IMPRINT",FACE,{"disambiguationData":[TD([[makeQuery(id+"F4.imprint","IMPRINT",EDGE,{"disambiguationData":[TD([[subQ2,1.0]])],"derivedFrom":subQ1}),1.0]])]});}
            var Q15;
            {var subQ0=sQuery(id+"F4.wireOp",EDGE,"E41");var subQ1=sQuery(id+"F4.wireOp",EDGE,"E23");var subQ2=makeQuery(id+"F4.imprint","INTERSECT",VERTEX,{"disambiguationData":[OD(1.0)],"derivedFrom":[subQ1,subQ0]});Q15=makeQuery(id+"F4.imprint","IMPRINT",FACE,{"disambiguationData":[TD([[makeQuery(id+"F4.imprint","IMPRINT",EDGE,{"disambiguationData":[TD([[subQ2,1.0]])],"derivedFrom":subQ1}),1.0]])]});}
            var Q16;
            {var subQ0=sQuery(id+"F4.wireOp",EDGE,"E41");var subQ1=sQuery(id+"F4.wireOp",EDGE,"E23");var subQ2=makeQuery(id+"F4.imprint","INTERSECT",VERTEX,{"disambiguationData":[OD(0.0)],"derivedFrom":[subQ1,subQ0]});Q16=makeQuery(id+"F4.imprint","IMPRINT",FACE,{"disambiguationData":[TD([[makeQuery(id+"F4.imprint","IMPRINT",EDGE,{"disambiguationData":[TD([[subQ2,-1.0]])],"derivedFrom":subQ1}),1.0]])]});}
            var Q17;
            {var subQ0=sQuery(id+"F4.wireOp",EDGE,"E41");var subQ1=sQuery(id+"F4.wireOp",EDGE,"E24");var subQ2=makeQuery(id+"F4.imprint","INTERSECT",VERTEX,{"disambiguationData":[OD(0.0)],"derivedFrom":[subQ1,subQ0]});Q17=makeQuery(id+"F4.imprint","IMPRINT",FACE,{"disambiguationData":[TD([[makeQuery(id+"F4.imprint","IMPRINT",EDGE,{"disambiguationData":[TD([[subQ2,-1.0]])],"derivedFrom":subQ1}),1.0]])]});}
            var Q18;
            {var subQ0=sQuery(id+"F4.wireOp",EDGE,"E41");var subQ1=sQuery(id+"F4.wireOp",EDGE,"E23");var subQ2=makeQuery(id+"F4.imprint","INTERSECT",VERTEX,{"disambiguationData":[OD(0.0)],"derivedFrom":[subQ1,subQ0]});Q18=makeQuery(id+"F4.imprint","IMPRINT",FACE,{"disambiguationData":[TD([[makeQuery(id+"F4.imprint","IMPRINT",EDGE,{"disambiguationData":[TD([[subQ2,-1.0]])],"derivedFrom":subQ1}),-1.0]])]});}
            var Q19;
            {var subQ0=sQuery(id+"F4.wireOp",EDGE,"E33");var subQ1=sQuery(id+"F4.wireOp",EDGE,"E23");var subQ2=makeQuery(id+"F4.imprint","INTERSECT",VERTEX,{"disambiguationData":[OD(1.0)],"derivedFrom":[subQ1,subQ0]});Q19=makeQuery(id+"F4.imprint","IMPRINT",FACE,{"disambiguationData":[TD([[makeQuery(id+"F4.imprint","IMPRINT",EDGE,{"disambiguationData":[TD([[subQ2,-1.0]])],"derivedFrom":subQ1}),1.0]])]});}
            var Q20;
            {var subQ0=sQuery(id+"F4.wireOp",EDGE,"E34.bottom");Q20=makeQuery(id+"F4.imprint","IMPRINT",FACE,{"disambiguationData":[TD([[makeQuery(id+"F4.imprint","IMPRINT",EDGE,{"derivedFrom":subQ0}),1.0]])]});}
            var Q21;
            {var subQ3=sQuery(id+"F4.wireOp",EDGE,"E24");var subQ5=sQuery(id+"F4.wireOp",EDGE,"E33");var subQ7=makeQuery(id+"F4.imprint","INTERSECT",VERTEX,{"disambiguationData":[OD(0.0)],"derivedFrom":[subQ3,subQ5]});Q21=makeQuery(id+"F4.imprint","IMPRINT",FACE,{"disambiguationData":[TD([[makeQuery(id+"F4.imprint","IMPRINT",EDGE,{"disambiguationData":[TD([[subQ7,-1.0]])],"derivedFrom":subQ3}),1.0]])]});}
            var Q22;
            {var subQ0=sQuery(id+"F4.wireOp",EDGE,"E35");var subQ1=sQuery(id+"F4.wireOp",EDGE,"E23");var subQ2=makeQuery(id+"F4.imprint","INTERSECT",VERTEX,{"disambiguationData":[OD(1.0)],"derivedFrom":[subQ1,subQ0]});Q22=makeQuery(id+"F4.imprint","IMPRINT",FACE,{"disambiguationData":[TD([[makeQuery(id+"F4.imprint","IMPRINT",EDGE,{"disambiguationData":[TD([[subQ2,-1.0]])],"derivedFrom":subQ1}),1.0]])]});}
            var Q23;
            {var subQ0=sQuery(id+"F4.wireOp",EDGE,"E37");var subQ1=sQuery(id+"F4.wireOp",EDGE,"E23");var subQ2=makeQuery(id+"F4.imprint","INTERSECT",VERTEX,{"disambiguationData":[OD(1.0)],"derivedFrom":[subQ1,subQ0]});Q23=makeQuery(id+"F4.imprint","IMPRINT",FACE,{"disambiguationData":[TD([[makeQuery(id+"F4.imprint","IMPRINT",EDGE,{"disambiguationData":[TD([[subQ2,-1.0]])],"derivedFrom":subQ1}),1.0]])]});}
            var Q24;
            {var subQ0=sQuery(id+"F4.wireOp",EDGE,"E35");var subQ1=sQuery(id+"F4.wireOp",EDGE,"E23");var subQ2=makeQuery(id+"F4.imprint","INTERSECT",VERTEX,{"disambiguationData":[OD(0.0)],"derivedFrom":[subQ1,subQ0]});Q24=makeQuery(id+"F4.imprint","IMPRINT",FACE,{"disambiguationData":[TD([[makeQuery(id+"F4.imprint","IMPRINT",EDGE,{"disambiguationData":[TD([[subQ2,-1.0]])],"derivedFrom":subQ1}),-1.0]])]});}
            var Q25;
            {var subQ0=sQuery(id+"F4.wireOp",EDGE,"E35");var subQ1=sQuery(id+"F4.wireOp",EDGE,"E24");var subQ2=makeQuery(id+"F4.imprint","INTERSECT",VERTEX,{"disambiguationData":[OD(0.0)],"derivedFrom":[subQ1,subQ0]});Q25=makeQuery(id+"F4.imprint","IMPRINT",FACE,{"disambiguationData":[TD([[makeQuery(id+"F4.imprint","IMPRINT",EDGE,{"disambiguationData":[TD([[subQ2,-1.0]])],"derivedFrom":subQ1}),1.0]])]});}
            var Q26;
            {var subQ0=sQuery(id+"F4.wireOp",EDGE,"E33");var subQ1=sQuery(id+"F4.wireOp",EDGE,"E23");var subQ2=makeQuery(id+"F4.imprint","INTERSECT",VERTEX,{"disambiguationData":[OD(1.0)],"derivedFrom":[subQ1,subQ0]});Q26=makeQuery(id+"F4.imprint","IMPRINT",FACE,{"disambiguationData":[TD([[makeQuery(id+"F4.imprint","IMPRINT",EDGE,{"disambiguationData":[TD([[subQ2,1.0]])],"derivedFrom":subQ1}),1.0]])]});}
            var Q27;
            {var subQ0=sQuery(id+"F4.wireOp",EDGE,"E33");var subQ1=sQuery(id+"F4.wireOp",EDGE,"E23");var subQ2=makeQuery(id+"F4.imprint","INTERSECT",VERTEX,{"disambiguationData":[OD(0.0)],"derivedFrom":[subQ1,subQ0]});Q27=makeQuery(id+"F4.imprint","IMPRINT",FACE,{"disambiguationData":[TD([[makeQuery(id+"F4.imprint","IMPRINT",EDGE,{"disambiguationData":[TD([[subQ2,-1.0]])],"derivedFrom":subQ1}),1.0]])]});}
            var Q28;
            {var subQ0=sQuery(id+"F4.wireOp",EDGE,"E35");var subQ1=sQuery(id+"F4.wireOp",EDGE,"E23");var subQ2=makeQuery(id+"F4.imprint","INTERSECT",VERTEX,{"disambiguationData":[OD(0.0)],"derivedFrom":[subQ1,subQ0]});Q28=makeQuery(id+"F4.imprint","IMPRINT",FACE,{"disambiguationData":[TD([[makeQuery(id+"F4.imprint","IMPRINT",EDGE,{"disambiguationData":[TD([[subQ2,-1.0]])],"derivedFrom":subQ1}),1.0]])]});}
            var Q29;
            {var subQ0=sQuery(id+"F4.wireOp",EDGE,"E35");var subQ1=sQuery(id+"F4.wireOp",EDGE,"E23");var subQ2=makeQuery(id+"F4.imprint","INTERSECT",VERTEX,{"disambiguationData":[OD(1.0)],"derivedFrom":[subQ1,subQ0]});Q29=makeQuery(id+"F4.imprint","IMPRINT",FACE,{"disambiguationData":[TD([[makeQuery(id+"F4.imprint","IMPRINT",EDGE,{"disambiguationData":[TD([[subQ2,1.0]])],"derivedFrom":subQ1}),1.0]])]});}
            var Q30;
            {var subQ1=sQuery(id+"F4.wireOp",EDGE,"E24");var subQ4=sQuery(id+"F4.wireOp",EDGE,"E39");var subQ14=makeQuery(id+"F4.imprint","INTERSECT",VERTEX,{"disambiguationData":[OD(1.0)],"derivedFrom":[subQ1,subQ4]});Q30=makeQuery(id+"F4.imprint","IMPRINT",FACE,{"disambiguationData":[TD([[makeQuery(id+"F4.imprint","IMPRINT",EDGE,{"disambiguationData":[TD([[subQ14,-1.0]])],"derivedFrom":subQ1}),1.0]])]});}
            extrude(context, id + "F8", {"entities" : qUnion([Q0, Q1, Q2, Q3, Q4, Q5, Q6, Q7, Q8, Q9, Q10, Q11, Q12, Q13, Q14, Q15, Q16, Q17, Q18, Q19, Q20, Q21, Q22, Q23, Q24, Q25, Q26, Q27, Q28, Q29, Q30]), "operationType" : NewBodyOperationType.ADD, "depth" : 1 * mm, "offsetDistance" : 25 * mm});
        }
        {
            var Q0;
            Q0=makeQuery(id+"F6.opExtrude","CAP_EDGE",EDGE,{"disambiguationData":[OSD([sQuery(id+"F4.wireOp",EDGE,"E32")])],"isStart":false});
            var Q1;
            Q1=makeQuery(id+"F6.opExtrude","CAP_FACE",FACE,{"disambiguationData":[OSD([sQuery(id+"F4.wireOp",EDGE,"E42")])],"isStart":false});
            var Q2;
            Q2=makeQuery(id+"F6.opExtrude","CAP_FACE",FACE,{"disambiguationData":[OSD([sQuery(id+"F4.wireOp",EDGE,"E40")])],"isStart":false});
            var Q3;
            Q3=makeQuery(id+"F6.opExtrude","CAP_FACE",FACE,{"disambiguationData":[OSD([sQuery(id+"F4.wireOp",EDGE,"E38")])],"isStart":false});
            var Q4;
            Q4=makeQuery(id+"F6.opExtrude","CAP_FACE",FACE,{"disambiguationData":[OSD([sQuery(id+"F4.wireOp",EDGE,"E36")])],"isStart":false});
            fillet(context, id + "F9", {"entities" : qUnion([Q0, Q1, Q2, Q3, Q4]), "radius" : 1 * mm, "tangentPropagation" : true, "allowEdgeOverflow" : false});
        }
        {
            var Q0;
            Q0=makeQuery(id+"F6.opExtrude","CAP_EDGE",EDGE,{"disambiguationData":[OSD([sQuery(id+"F4.wireOp",EDGE,"E34.top")])],"isStart":false});
            var Q1;
            Q1=makeQuery(id+"F6.opExtrude","CAP_EDGE",EDGE,{"disambiguationData":[OSD([sQuery(id+"F4.wireOp",EDGE,"E34.left")])],"isStart":false});
            var Q2;
            Q2=makeQuery(id+"F6.opExtrude","CAP_EDGE",EDGE,{"disambiguationData":[OSD([sQuery(id+"F4.wireOp",EDGE,"E34.bottom")])],"isStart":false});
            var Q3;
            Q3=makeQuery(id+"F6.opExtrude","CAP_EDGE",EDGE,{"disambiguationData":[OSD([sQuery(id+"F4.wireOp",EDGE,"E34.right")])],"isStart":false});
            fillet(context, id + "F10", {"entities" : qUnion([Q0, Q1, Q2, Q3]), "radius" : .8 * mm, "tangentPropagation" : true, "allowEdgeOverflow" : false});
        }
        {
            var Q0;
            Q0=qCreatedBy(makeId("Top.planeOp"),FACE);
            var sketch = newSketch(context, id + "F11", { "sketchPlane" : qUnion([Q0])});
            skCircle(sketch, "E43", {"center": v(0, 0) * mm, "radius": 48 * mm});
            skSolve(sketch);
        }
        {
            var Q0;
            Q0=makeQuery(id+"F11.imprint","IMPRINT",FACE,{"disambiguationData":[TD([[makeQuery(id+"F11.imprint","IMPRINT",EDGE,{"derivedFrom":sQuery(id+"F11.wireOp",EDGE,"E43")}),1.0]])]});
            var Q1;
            {var subQ0=sQuery(id+"F0.wireOp",EDGE,"E17.right");var subQ1=sQuery(id+"F0.wireOp",EDGE,"E0");var subQ2=makeQuery(id+"F0.imprint","INTERSECT",VERTEX,{"disambiguationData":[OD(0.0)],"derivedFrom":[subQ1,subQ0]});Q1=makeQuery(id+"F0.imprint","IMPRINT",FACE,{"disambiguationData":[TD([[makeQuery(id+"F0.imprint","IMPRINT",EDGE,{"disambiguationData":[TD([[subQ2,-1.0]])],"derivedFrom":subQ1}),1.0]])]});}
            extrude(context, id + "F12", {"entities" : qUnion([Q0, Q1]), "operationType" : NewBodyOperationType.REMOVE, "depth" : 2 * mm, "offsetDistance" : 25 * mm});
        }
    });
